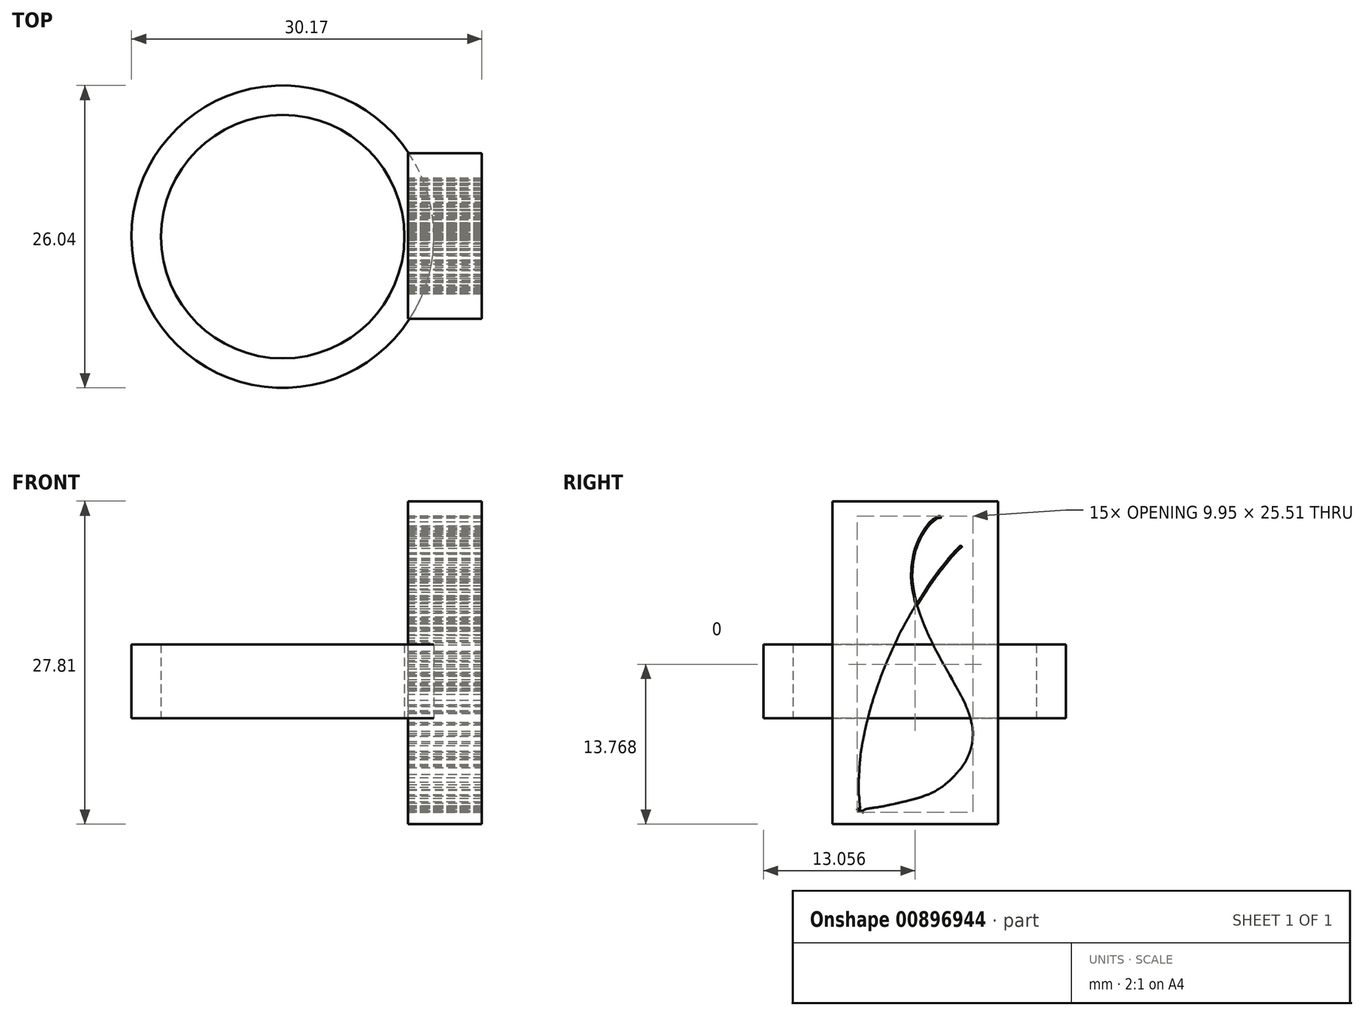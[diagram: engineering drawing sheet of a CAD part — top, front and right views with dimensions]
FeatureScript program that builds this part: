
annotation { "Feature Type Name" : "Feature", "Feature Type Description" : "" }
export const myFeature = defineFeature(function(context is Context, id is Id, definition is map)
    precondition{}
    {
        {
            var Q0;
            Q0=qCreatedBy(makeId("Top.planeOp"),FACE);
            var sketch = newSketch(context, id + "F0", { "sketchPlane" : qUnion([Q0])});
            skCircle(sketch, "E0", {"center": v(0, 0) * mm, "radius": 10.48 * mm});
            skCircle(sketch, "E1", {"center": v(0, 0) * mm, "radius": 13.02 * mm});
            skSolve(sketch);
        }
        {
            var Q0;
            Q0 = qSketchRegion(id + "F0", true);
            extrude(context, id + "F1", {"entities" : qUnion([Q0]), "depth" : 6.35 * mm, "offsetDistance" : 25.4 * mm});
        }
        {
            var Q0;
            Q0=qCreatedBy(makeId("Right.planeOp"),FACE);
            var sketch = newSketch(context, id + "F2", { "sketchPlane" : qUnion([Q0])});
            skLineSegment(sketch, "E2", {"start": v(0.02, 4.98) * mm, "end": v(0.1, 5.1) * mm});
            skLineSegment(sketch, "E3", {"start": v(0.1, 5.1) * mm, "end": v(0.07, 5.2) * mm});
            skLineSegment(sketch, "E4", {"start": v(0.07, 5.2) * mm, "end": v(0.02, 4.98) * mm});
            skLineSegment(sketch, "E5", {"start": v(-4.25, -12.47) * mm, "end": v(-4.48, -12.52) * mm});
            skLineSegment(sketch, "E6", {"start": v(-4.48, -12.52) * mm, "end": v(-4.48, -12.6) * mm});
            skLineSegment(sketch, "E7", {"start": v(-4.48, -12.6) * mm, "end": v(-4.25, -12.47) * mm});
            skFitSpline(sketch, "E8", {"points": [v(-4.5, -12.72) * mm, v(-4.5, -12.7) * mm, v(-4.52, -12.7) * mm, v(-4.52, -12.68) * mm]});
            skFitSpline(sketch, "E9", {"points": [v(-4.52, -12.68) * mm, v(-4.52, -12.67) * mm, v(-4.53, -12.66) * mm, v(-4.55, -12.65) * mm]});
            skFitSpline(sketch, "E10", {"points": [v(-4.55, -12.65) * mm, v(-4.57, -12.64) * mm, v(-4.6, -12.61) * mm, v(-4.62, -12.58) * mm]});
            skFitSpline(sketch, "E11", {"points": [v(-4.62, -12.58) * mm, v(-4.66, -12.53) * mm, v(-4.66, -12.52) * mm, v(-4.71, -12.55) * mm]});
            skFitSpline(sketch, "E12", {"points": [v(-4.71, -12.55) * mm, v(-4.76, -12.56) * mm, v(-4.75, -12.6) * mm, v(-4.7, -12.63) * mm]});
            skFitSpline(sketch, "E13", {"points": [v(-4.7, -12.63) * mm, v(-4.65, -12.64) * mm, v(-4.65, -12.67) * mm, v(-4.68, -12.69) * mm]});
            skFitSpline(sketch, "E14", {"points": [v(-4.68, -12.69) * mm, v(-4.7, -12.7) * mm, v(-4.73, -12.67) * mm, v(-4.77, -12.65) * mm]});
            skFitSpline(sketch, "E15", {"points": [v(-4.77, -12.65) * mm, v(-4.8, -12.62) * mm, v(-4.85, -12.59) * mm, v(-4.88, -12.57) * mm]});
            skFitSpline(sketch, "E16", {"points": [v(-4.88, -12.57) * mm, v(-4.92, -12.55) * mm, v(-4.94, -12.53) * mm, v(-4.94, -12.5) * mm]});
            skFitSpline(sketch, "E17", {"points": [v(-4.94, -12.5) * mm, v(-4.94, -12.46) * mm, v(-4.93, -12.45) * mm, v(-4.8, -12.41) * mm]});
            skFitSpline(sketch, "E18", {"points": [v(-4.8, -12.41) * mm, v(-4.7, -12.38) * mm, v(-4.69, -12.37) * mm, v(-4.72, -12.22) * mm]});
            skFitSpline(sketch, "E19", {"points": [v(-4.72, -12.22) * mm, v(-4.73, -12.16) * mm, v(-4.75, -11.95) * mm, v(-4.76, -11.75) * mm]});
            skFitSpline(sketch, "E20", {"points": [v(-4.76, -11.75) * mm, v(-4.77, -11.56) * mm, v(-4.78, -11.36) * mm, v(-4.8, -11.3) * mm]});
            skFitSpline(sketch, "E21", {"points": [v(-4.8, -11.3) * mm, v(-4.81, -11.17) * mm, v(-4.82, -10.04) * mm, v(-4.8, -9.78) * mm]});
            skFitSpline(sketch, "E22", {"points": [v(-4.8, -9.78) * mm, v(-4.8, -9.6) * mm, v(-4.79, -9.5) * mm, v(-4.76, -9.07) * mm]});
            skFitSpline(sketch, "E23", {"points": [v(-4.76, -9.07) * mm, v(-4.75, -8.84) * mm, v(-4.73, -8.53) * mm, v(-4.7, -8.34) * mm]});
            skFitSpline(sketch, "E24", {"points": [v(-4.7, -8.34) * mm, v(-4.7, -8.25) * mm, v(-4.69, -8.1) * mm, v(-4.68, -8) * mm]});
            skFitSpline(sketch, "E25", {"points": [v(-4.68, -8) * mm, v(-4.67, -7.89) * mm, v(-4.66, -7.78) * mm, v(-4.65, -7.75) * mm]});
            skFitSpline(sketch, "E26", {"points": [v(-4.65, -7.75) * mm, v(-4.65, -7.72) * mm, v(-4.64, -7.63) * mm, v(-4.63, -7.55) * mm]});
            skFitSpline(sketch, "E27", {"points": [v(-4.63, -7.55) * mm, v(-4.62, -7.47) * mm, v(-4.6, -7.34) * mm, v(-4.58, -7.25) * mm]});
            skFitSpline(sketch, "E28", {"points": [v(-4.58, -7.25) * mm, v(-4.56, -7.17) * mm, v(-4.54, -7.05) * mm, v(-4.53, -6.98) * mm]});
            skFitSpline(sketch, "E29", {"points": [v(-4.53, -6.98) * mm, v(-4.52, -6.91) * mm, v(-4.51, -6.83) * mm, v(-4.5, -6.8) * mm]});
            skFitSpline(sketch, "E30", {"points": [v(-4.5, -6.8) * mm, v(-4.5, -6.77) * mm, v(-4.48, -6.7) * mm, v(-4.47, -6.63) * mm]});
            skFitSpline(sketch, "E31", {"points": [v(-4.47, -6.63) * mm, v(-4.44, -6.51) * mm, v(-4.43, -6.46) * mm, v(-4.39, -6.23) * mm]});
            skFitSpline(sketch, "E32", {"points": [v(-4.39, -6.23) * mm, v(-4.38, -6.18) * mm, v(-4.36, -6.12) * mm, v(-4.36, -6.1) * mm]});
            skFitSpline(sketch, "E33", {"points": [v(-4.36, -6.1) * mm, v(-4.35, -6.07) * mm, v(-4.34, -6) * mm, v(-4.33, -5.95) * mm]});
            skFitSpline(sketch, "E34", {"points": [v(-4.33, -5.95) * mm, v(-4.33, -5.9) * mm, v(-4.31, -5.81) * mm, v(-4.3, -5.76) * mm]});
            skFitSpline(sketch, "E35", {"points": [v(-4.3, -5.76) * mm, v(-4.28, -5.68) * mm, v(-4.25, -5.55) * mm, v(-4.18, -5.24) * mm]});
            skFitSpline(sketch, "E36", {"points": [v(-4.18, -5.24) * mm, v(-4.16, -5.15) * mm, v(-4.13, -5.02) * mm, v(-4.1, -4.94) * mm]});
            skFitSpline(sketch, "E37", {"points": [v(-4.1, -4.94) * mm, v(-4.05, -4.75) * mm, v(-3.99, -4.47) * mm, v(-3.98, -4.4) * mm]});
            skFitSpline(sketch, "E38", {"points": [v(-3.98, -4.4) * mm, v(-3.97, -4.38) * mm, v(-3.96, -4.35) * mm, v(-3.95, -4.35) * mm]});
            skFitSpline(sketch, "E39", {"points": [v(-3.95, -4.35) * mm, v(-3.95, -4.34) * mm, v(-3.94, -4.32) * mm, v(-3.94, -4.3) * mm]});
            skFitSpline(sketch, "E40", {"points": [v(-3.94, -4.3) * mm, v(-3.94, -4.28) * mm, v(-3.93, -4.25) * mm, v(-3.93, -4.22) * mm]});
            skFitSpline(sketch, "E41", {"points": [v(-3.93, -4.22) * mm, v(-3.92, -4.2) * mm, v(-3.9, -4.16) * mm, v(-3.9, -4.12) * mm]});
            skFitSpline(sketch, "E42", {"points": [v(-3.9, -4.12) * mm, v(-3.89, -4.09) * mm, v(-3.86, -4) * mm, v(-3.84, -3.92) * mm]});
            skFitSpline(sketch, "E43", {"points": [v(-3.84, -3.92) * mm, v(-3.82, -3.84) * mm, v(-3.78, -3.71) * mm, v(-3.76, -3.64) * mm]});
            skFitSpline(sketch, "E44", {"points": [v(-3.76, -3.64) * mm, v(-3.74, -3.56) * mm, v(-3.72, -3.49) * mm, v(-3.72, -3.48) * mm]});
            skFitSpline(sketch, "E45", {"points": [v(-3.72, -3.48) * mm, v(-3.64, -3.26) * mm, v(-3.6, -3.14) * mm, v(-3.6, -3.12) * mm]});
            skFitSpline(sketch, "E46", {"points": [v(-3.6, -3.12) * mm, v(-3.6, -3.1) * mm, v(-3.47, -2.68) * mm, v(-3.44, -2.6) * mm]});
            skFitSpline(sketch, "E47", {"points": [v(-3.44, -2.6) * mm, v(-3.4, -2.52) * mm, v(-3.34, -2.32) * mm, v(-3.33, -2.26) * mm]});
            skFitSpline(sketch, "E48", {"points": [v(-3.33, -2.26) * mm, v(-3.32, -2.22) * mm, v(-3.3, -2.17) * mm, v(-3.29, -2.15) * mm]});
            skFitSpline(sketch, "E49", {"points": [v(-3.29, -2.15) * mm, v(-3.28, -2.13) * mm, v(-3.27, -2.1) * mm, v(-3.27, -2.09) * mm]});
            skFitSpline(sketch, "E50", {"points": [v(-3.27, -2.09) * mm, v(-3.27, -2.07) * mm, v(-3.26, -2.04) * mm, v(-3.25, -2.02) * mm]});
            skFitSpline(sketch, "E51", {"points": [v(-3.25, -2.02) * mm, v(-3.24, -2) * mm, v(-3.21, -1.92) * mm, v(-3.18, -1.84) * mm]});
            skFitSpline(sketch, "E52", {"points": [v(-3.18, -1.84) * mm, v(-3.15, -1.75) * mm, v(-3.08, -1.54) * mm, v(-3.02, -1.37) * mm]});
            skFitSpline(sketch, "E53", {"points": [v(-3.02, -1.37) * mm, v(-2.96, -1.2) * mm, v(-2.9, -1.04) * mm, v(-2.9, -1.01) * mm]});
            skFitSpline(sketch, "E54", {"points": [v(-2.9, -1.01) * mm, v(-2.89, -0.98) * mm, v(-2.87, -0.95) * mm, v(-2.87, -0.94) * mm]});
            skFitSpline(sketch, "E55", {"points": [v(-2.87, -0.94) * mm, v(-2.86, -0.93) * mm, v(-2.85, -0.92) * mm, v(-2.85, -0.9) * mm]});
            skFitSpline(sketch, "E56", {"points": [v(-2.85, -0.9) * mm, v(-2.85, -0.9) * mm, v(-2.84, -0.84) * mm, v(-2.81, -0.8) * mm]});
            skFitSpline(sketch, "E57", {"points": [v(-2.81, -0.8) * mm, v(-2.8, -0.75) * mm, v(-2.75, -0.66) * mm, v(-2.73, -0.58) * mm]});
            skFitSpline(sketch, "E58", {"points": [v(-2.73, -0.58) * mm, v(-2.7, -0.5) * mm, v(-2.66, -0.41) * mm, v(-2.64, -0.37) * mm]});
            skFitSpline(sketch, "E59", {"points": [v(-2.64, -0.37) * mm, v(-2.62, -0.33) * mm, v(-2.6, -0.26) * mm, v(-2.58, -0.22) * mm]});
            skFitSpline(sketch, "E60", {"points": [v(-2.58, -0.22) * mm, v(-2.55, -0.15) * mm, v(-2.47, 0.05) * mm, v(-2.39, 0.23) * mm]});
            skFitSpline(sketch, "E61", {"points": [v(-2.39, 0.23) * mm, v(-2.37, 0.27) * mm, v(-2.36, 0.3) * mm, v(-2.36, 0.31) * mm]});
            skFitSpline(sketch, "E62", {"points": [v(-2.36, 0.31) * mm, v(-2.36, 0.32) * mm, v(-2.34, 0.35) * mm, v(-2.32, 0.38) * mm]});
            skFitSpline(sketch, "E63", {"points": [v(-2.32, 0.38) * mm, v(-2.3, 0.42) * mm, v(-2.28, 0.48) * mm, v(-2.26, 0.53) * mm]});
            skFitSpline(sketch, "E64", {"points": [v(-2.26, 0.53) * mm, v(-2.24, 0.57) * mm, v(-2.2, 0.66) * mm, v(-2.16, 0.74) * mm]});
            skFitSpline(sketch, "E65", {"points": [v(-2.16, 0.74) * mm, v(-2.13, 0.8) * mm, v(-2.1, 0.87) * mm, v(-2.1, 0.88) * mm]});
            skFitSpline(sketch, "E66", {"points": [v(-2.1, 0.88) * mm, v(-2.1, 0.9) * mm, v(-2.09, 0.91) * mm, v(-2.08, 0.92) * mm]});
            skFitSpline(sketch, "E67", {"points": [v(-2.08, 0.92) * mm, v(-2.06, 0.93) * mm, v(-2.06, 0.95) * mm, v(-2.06, 0.96) * mm]});
            skFitSpline(sketch, "E68", {"points": [v(-2.06, 0.96) * mm, v(-2.07, 0.96) * mm, v(-2.06, 0.98) * mm, v(-2.05, 1) * mm]});
            skFitSpline(sketch, "E69", {"points": [v(-2.05, 1) * mm, v(-2.05, 1.01) * mm, v(-2.01, 1.08) * mm, v(-1.98, 1.15) * mm]});
            skFitSpline(sketch, "E70", {"points": [v(-1.98, 1.15) * mm, v(-1.9, 1.33) * mm, v(-1.88, 1.38) * mm, v(-1.77, 1.61) * mm]});
            skFitSpline(sketch, "E71", {"points": [v(-1.77, 1.61) * mm, v(-1.72, 1.72) * mm, v(-1.66, 1.84) * mm, v(-1.64, 1.88) * mm]});
            skFitSpline(sketch, "E72", {"points": [v(-1.64, 1.88) * mm, v(-1.63, 1.92) * mm, v(-1.6, 1.97) * mm, v(-1.6, 1.98) * mm]});
            skFitSpline(sketch, "E73", {"points": [v(-1.6, 1.98) * mm, v(-1.58, 2) * mm, v(-1.57, 2) * mm, v(-1.57, 2.02) * mm]});
            skFitSpline(sketch, "E74", {"points": [v(-1.57, 2.02) * mm, v(-1.57, 2.02) * mm, v(-1.55, 2.07) * mm, v(-1.52, 2.13) * mm]});
            skFitSpline(sketch, "E75", {"points": [v(-1.52, 2.13) * mm, v(-1.5, 2.19) * mm, v(-1.48, 2.24) * mm, v(-1.48, 2.25) * mm]});
            skFitSpline(sketch, "E76", {"points": [v(-1.48, 2.25) * mm, v(-1.48, 2.25) * mm, v(-1.23, 2.76) * mm, v(-1.2, 2.82) * mm]});
            skFitSpline(sketch, "E77", {"points": [v(-1.2, 2.82) * mm, v(-1.2, 2.84) * mm, v(-1.16, 2.9) * mm, v(-1.14, 2.94) * mm]});
            skFitSpline(sketch, "E78", {"points": [v(-1.14, 2.94) * mm, v(-1.1, 2.99) * mm, v(-1.08, 3.05) * mm, v(-1.06, 3.07) * mm]});
            skFitSpline(sketch, "E79", {"points": [v(-1.06, 3.07) * mm, v(-1.04, 3.1) * mm, v(-1.03, 3.12) * mm, v(-1.03, 3.13) * mm]});
            skFitSpline(sketch, "E80", {"points": [v(-1.03, 3.13) * mm, v(-1.03, 3.15) * mm, v(-1.02, 3.16) * mm, v(-1.01, 3.17) * mm]});
            skFitSpline(sketch, "E81", {"points": [v(-1.01, 3.17) * mm, v(-1, 3.2) * mm, v(-0.95, 3.27) * mm, v(-0.85, 3.46) * mm]});
            skFitSpline(sketch, "E82", {"points": [v(-0.85, 3.46) * mm, v(-0.8, 3.55) * mm, v(-0.75, 3.65) * mm, v(-0.72, 3.7) * mm]});
            skFitSpline(sketch, "E83", {"points": [v(-0.72, 3.7) * mm, v(-0.69, 3.75) * mm, v(-0.66, 3.8) * mm, v(-0.66, 3.8) * mm]});
            skFitSpline(sketch, "E84", {"points": [v(-0.66, 3.8) * mm, v(-0.66, 3.8) * mm, v(-0.63, 3.87) * mm, v(-0.59, 3.93) * mm]});
            skFitSpline(sketch, "E85", {"points": [v(-0.59, 3.93) * mm, v(-0.55, 4) * mm, v(-0.5, 4.08) * mm, v(-0.49, 4.1) * mm]});
            skFitSpline(sketch, "E86", {"points": [v(-0.49, 4.1) * mm, v(-0.44, 4.19) * mm, v(-0.36, 4.35) * mm, v(-0.34, 4.37) * mm]});
            skFitSpline(sketch, "E87", {"points": [v(-0.34, 4.37) * mm, v(-0.33, 4.38) * mm, v(-0.31, 4.42) * mm, v(-0.29, 4.46) * mm]});
            skFitSpline(sketch, "E88", {"points": [v(-0.29, 4.46) * mm, v(-0.2, 4.62) * mm, v(-0.16, 4.7) * mm, v(-0.1, 4.77) * mm]});
            skFitSpline(sketch, "E89", {"points": [v(-0.1, 4.77) * mm, v(-0.08, 4.8) * mm, v(-0.05, 4.85) * mm, v(-0.05, 4.85) * mm]});
            skFitSpline(sketch, "E90", {"points": [v(-0.05, 4.85) * mm, v(-0.05, 4.85) * mm, v(-0.02, 4.91) * mm, v(0.02, 4.98) * mm]});
            skFitSpline(sketch, "E91", {"points": [v(0.07, 5.2) * mm, v(0.05, 5.27) * mm, v(0.04, 5.34) * mm, v(0.03, 5.37) * mm]});
            skFitSpline(sketch, "E92", {"points": [v(0.03, 5.37) * mm, v(-0.01, 5.5) * mm, v(-0.04, 5.63) * mm, v(-0.04, 5.68) * mm]});
            skFitSpline(sketch, "E93", {"points": [v(-0.04, 5.68) * mm, v(-0.04, 5.72) * mm, v(-0.05, 5.75) * mm, v(-0.06, 5.76) * mm]});
            skFitSpline(sketch, "E94", {"points": [v(-0.06, 5.76) * mm, v(-0.07, 5.76) * mm, v(-0.07, 5.8) * mm, v(-0.07, 5.83) * mm]});
            skFitSpline(sketch, "E95", {"points": [v(-0.07, 5.83) * mm, v(-0.07, 5.86) * mm, v(-0.08, 5.9) * mm, v(-0.09, 5.93) * mm]});
            skFitSpline(sketch, "E96", {"points": [v(-0.09, 5.93) * mm, v(-0.1, 5.95) * mm, v(-0.1, 6) * mm, v(-0.1, 6.03) * mm]});
            skFitSpline(sketch, "E97", {"points": [v(-0.1, 6.03) * mm, v(-0.11, 6.06) * mm, v(-0.13, 6.12) * mm, v(-0.14, 6.15) * mm]});
            skFitSpline(sketch, "E98", {"points": [v(-0.14, 6.15) * mm, v(-0.16, 6.18) * mm, v(-0.16, 6.2) * mm, v(-0.16, 6.22) * mm]});
            skFitSpline(sketch, "E99", {"points": [v(-0.16, 6.22) * mm, v(-0.15, 6.22) * mm, v(-0.16, 6.27) * mm, v(-0.17, 6.32) * mm]});
            skFitSpline(sketch, "E100", {"points": [v(-0.17, 6.32) * mm, v(-0.18, 6.36) * mm, v(-0.2, 6.4) * mm, v(-0.19, 6.41) * mm]});
            skFitSpline(sketch, "E101", {"points": [v(-0.19, 6.41) * mm, v(-0.18, 6.42) * mm, v(-0.19, 6.44) * mm, v(-0.2, 6.47) * mm]});
            skFitSpline(sketch, "E102", {"points": [v(-0.2, 6.47) * mm, v(-0.21, 6.5) * mm, v(-0.23, 6.6) * mm, v(-0.23, 6.71) * mm]});
            skFitSpline(sketch, "E103", {"points": [v(-0.23, 6.71) * mm, v(-0.23, 6.74) * mm, v(-0.24, 6.76) * mm, v(-0.25, 6.76) * mm]});
            skFitSpline(sketch, "E104", {"points": [v(-0.25, 6.76) * mm, v(-0.25, 6.77) * mm, v(-0.26, 6.83) * mm, v(-0.27, 6.9) * mm]});
            skFitSpline(sketch, "E105", {"points": [v(-0.27, 6.9) * mm, v(-0.29, 7.23) * mm, v(-0.3, 7.32) * mm, v(-0.3, 7.34) * mm]});
            skFitSpline(sketch, "E106", {"points": [v(-0.3, 7.34) * mm, v(-0.32, 7.38) * mm, v(-0.3, 7.89) * mm, v(-0.28, 8.17) * mm]});
            skFitSpline(sketch, "E107", {"points": [v(-0.28, 8.17) * mm, v(-0.28, 8.24) * mm, v(-0.27, 8.31) * mm, v(-0.28, 8.34) * mm]});
            skFitSpline(sketch, "E108", {"points": [v(-0.28, 8.34) * mm, v(-0.28, 8.37) * mm, v(-0.27, 8.46) * mm, v(-0.25, 8.54) * mm]});
            skFitSpline(sketch, "E109", {"points": [v(-0.25, 8.54) * mm, v(-0.24, 8.62) * mm, v(-0.22, 8.73) * mm, v(-0.22, 8.77) * mm]});
            skFitSpline(sketch, "E110", {"points": [v(-0.22, 8.77) * mm, v(-0.22, 8.81) * mm, v(-0.2, 8.89) * mm, v(-0.2, 8.94) * mm]});
            skFitSpline(sketch, "E111", {"points": [v(-0.2, 8.94) * mm, v(-0.19, 8.99) * mm, v(-0.17, 9.07) * mm, v(-0.16, 9.13) * mm]});
            skFitSpline(sketch, "E112", {"points": [v(-0.16, 9.13) * mm, v(-0.13, 9.4) * mm, v(-0.1, 9.57) * mm, v(-0.08, 9.6) * mm]});
            skFitSpline(sketch, "E113", {"points": [v(-0.08, 9.6) * mm, v(-0.07, 9.6) * mm, v(-0.07, 9.63) * mm, v(-0.06, 9.65) * mm]});
            skFitSpline(sketch, "E114", {"points": [v(-0.06, 9.65) * mm, v(-0.05, 9.72) * mm, v(0.1, 10.2) * mm, v(0.14, 10.3) * mm]});
            skFitSpline(sketch, "E115", {"points": [v(0.14, 10.3) * mm, v(0.16, 10.33) * mm, v(0.18, 10.39) * mm, v(0.2, 10.43) * mm]});
            skFitSpline(sketch, "E116", {"points": [v(0.2, 10.43) * mm, v(0.28, 10.64) * mm, v(0.4, 10.9) * mm, v(0.48, 11.03) * mm]});
            skFitSpline(sketch, "E117", {"points": [v(0.48, 11.03) * mm, v(0.5, 11.07) * mm, v(0.55, 11.15) * mm, v(0.57, 11.2) * mm]});
            skFitSpline(sketch, "E118", {"points": [v(0.57, 11.2) * mm, v(0.6, 11.25) * mm, v(0.65, 11.35) * mm, v(0.7, 11.4) * mm]});
            skFitSpline(sketch, "E119", {"points": [v(0.7, 11.4) * mm, v(0.73, 11.47) * mm, v(0.79, 11.56) * mm, v(0.82, 11.62) * mm]});
            skFitSpline(sketch, "E120", {"points": [v(0.82, 11.62) * mm, v(0.85, 11.67) * mm, v(0.9, 11.75) * mm, v(0.94, 11.79) * mm]});
            skFitSpline(sketch, "E121", {"points": [v(0.94, 11.79) * mm, v(0.97, 11.82) * mm, v(1.03, 11.9) * mm, v(1.06, 11.95) * mm]});
            skFitSpline(sketch, "E122", {"points": [v(1.06, 11.95) * mm, v(1.24, 12.18) * mm, v(1.67, 12.54) * mm, v(1.9, 12.66) * mm]});
            skFitSpline(sketch, "E123", {"points": [v(1.9, 12.66) * mm, v(1.94, 12.67) * mm, v(1.99, 12.7) * mm, v(2, 12.71) * mm]});
            skFitSpline(sketch, "E124", {"points": [v(2, 12.71) * mm, v(2.06, 12.76) * mm, v(2.24, 12.73) * mm, v(2.26, 12.67) * mm]});
            skFitSpline(sketch, "E125", {"points": [v(2.26, 12.67) * mm, v(2.27, 12.63) * mm, v(2.2, 12.59) * mm, v(2.15, 12.6) * mm]});
            skFitSpline(sketch, "E126", {"points": [v(2.15, 12.6) * mm, v(2.05, 12.61) * mm, v(1.8, 12.47) * mm, v(1.57, 12.27) * mm]});
            skFitSpline(sketch, "E127", {"points": [v(1.57, 12.27) * mm, v(1.46, 12.17) * mm, v(1.23, 11.94) * mm, v(1.15, 11.84) * mm]});
            skFitSpline(sketch, "E128", {"points": [v(1.15, 11.84) * mm, v(1.11, 11.8) * mm, v(1.06, 11.74) * mm, v(1.04, 11.7) * mm]});
            skFitSpline(sketch, "E129", {"points": [v(1.04, 11.7) * mm, v(1.01, 11.67) * mm, v(0.97, 11.61) * mm, v(0.95, 11.57) * mm]});
            skFitSpline(sketch, "E130", {"points": [v(0.95, 11.57) * mm, v(0.92, 11.52) * mm, v(0.9, 11.47) * mm, v(0.88, 11.46) * mm]});
            skFitSpline(sketch, "E131", {"points": [v(0.88, 11.46) * mm, v(0.87, 11.45) * mm, v(0.84, 11.41) * mm, v(0.82, 11.37) * mm]});
            skFitSpline(sketch, "E132", {"points": [v(0.82, 11.37) * mm, v(0.8, 11.33) * mm, v(0.76, 11.29) * mm, v(0.75, 11.28) * mm]});
            skFitSpline(sketch, "E133", {"points": [v(0.75, 11.28) * mm, v(0.74, 11.27) * mm, v(0.73, 11.24) * mm, v(0.72, 11.22) * mm]});
            skFitSpline(sketch, "E134", {"points": [v(0.72, 11.22) * mm, v(0.72, 11.2) * mm, v(0.7, 11.16) * mm, v(0.67, 11.14) * mm]});
            skFitSpline(sketch, "E135", {"points": [v(0.67, 11.14) * mm, v(0.65, 11.11) * mm, v(0.62, 11.05) * mm, v(0.6, 11) * mm]});
            skFitSpline(sketch, "E136", {"points": [v(0.6, 11) * mm, v(0.57, 10.95) * mm, v(0.53, 10.89) * mm, v(0.5, 10.85) * mm]});
            skFitSpline(sketch, "E137", {"points": [v(0.5, 10.85) * mm, v(0.5, 10.82) * mm, v(0.48, 10.78) * mm, v(0.48, 10.78) * mm]});
            skFitSpline(sketch, "E138", {"points": [v(0.48, 10.78) * mm, v(0.48, 10.77) * mm, v(0.46, 10.74) * mm, v(0.44, 10.71) * mm]});
            skFitSpline(sketch, "E139", {"points": [v(0.44, 10.71) * mm, v(0.43, 10.69) * mm, v(0.42, 10.67) * mm, v(0.42, 10.66) * mm]});
            skFitSpline(sketch, "E140", {"points": [v(0.42, 10.66) * mm, v(0.42, 10.66) * mm, v(0.4, 10.6) * mm, v(0.36, 10.53) * mm]});
            skFitSpline(sketch, "E141", {"points": [v(0.36, 10.53) * mm, v(0.33, 10.46) * mm, v(0.3, 10.4) * mm, v(0.3, 10.38) * mm]});
            skFitSpline(sketch, "E142", {"points": [v(0.3, 10.38) * mm, v(0.3, 10.36) * mm, v(0.29, 10.34) * mm, v(0.28, 10.32) * mm]});
            skFitSpline(sketch, "E143", {"points": [v(0.28, 10.32) * mm, v(0.26, 10.3) * mm, v(0.25, 10.28) * mm, v(0.25, 10.27) * mm]});
            skFitSpline(sketch, "E144", {"points": [v(0.25, 10.27) * mm, v(0.25, 10.26) * mm, v(0.24, 10.22) * mm, v(0.23, 10.2) * mm]});
            skFitSpline(sketch, "E145", {"points": [v(0.23, 10.2) * mm, v(0.22, 10.17) * mm, v(0.2, 10.12) * mm, v(0.19, 10.08) * mm]});
            skFitSpline(sketch, "E146", {"points": [v(0.19, 10.08) * mm, v(0.18, 10.05) * mm, v(0.16, 10) * mm, v(0.15, 9.99) * mm]});
            skFitSpline(sketch, "E147", {"points": [v(0.15, 9.99) * mm, v(0.12, 9.91) * mm, v(0.03, 9.62) * mm, v(0.03, 9.59) * mm]});
            skFitSpline(sketch, "E148", {"points": [v(0.03, 9.59) * mm, v(0.03, 9.57) * mm, v(0.02, 9.52) * mm, v(0, 9.49) * mm]});
            skFitSpline(sketch, "E149", {"points": [v(0, 9.49) * mm, v(0, 9.45) * mm, v(-0.03, 9.35) * mm, v(-0.04, 9.25) * mm]});
            skFitSpline(sketch, "E150", {"points": [v(-0.04, 9.25) * mm, v(-0.06, 9.16) * mm, v(-0.08, 9.05) * mm, v(-0.08, 9.01) * mm]});
            skFitSpline(sketch, "E151", {"points": [v(-0.08, 9.01) * mm, v(-0.12, 8.87) * mm, v(-0.18, 8.26) * mm, v(-0.2, 7.92) * mm]});
            skFitSpline(sketch, "E152", {"points": [v(-0.2, 7.92) * mm, v(-0.21, 7.62) * mm, v(-0.21, 7.53) * mm, v(-0.2, 7.25) * mm]});
            skFitSpline(sketch, "E153", {"points": [v(-0.2, 7.25) * mm, v(-0.18, 7.07) * mm, v(-0.15, 6.87) * mm, v(-0.14, 6.79) * mm]});
            skFitSpline(sketch, "E154", {"points": [v(-0.14, 6.79) * mm, v(-0.11, 6.6) * mm, v(-0.1, 6.55) * mm, v(-0.08, 6.42) * mm]});
            skFitSpline(sketch, "E155", {"points": [v(-0.08, 6.42) * mm, v(-0.08, 6.36) * mm, v(-0.06, 6.27) * mm, v(-0.05, 6.21) * mm]});
            skFitSpline(sketch, "E156", {"points": [v(-0.05, 6.21) * mm, v(0, 6.02) * mm, v(0.02, 5.92) * mm, v(0.01, 5.9) * mm]});
            skFitSpline(sketch, "E157", {"points": [v(0.01, 5.9) * mm, v(0.01, 5.9) * mm, v(0.01, 5.88) * mm, v(0.02, 5.87) * mm]});
            skFitSpline(sketch, "E158", {"points": [v(0.02, 5.87) * mm, v(0.03, 5.85) * mm, v(0.04, 5.83) * mm, v(0.04, 5.82) * mm]});
            skFitSpline(sketch, "E159", {"points": [v(0.04, 5.82) * mm, v(0.04, 5.8) * mm, v(0.06, 5.72) * mm, v(0.07, 5.63) * mm]});
            skFitSpline(sketch, "E160", {"points": [v(0.07, 5.63) * mm, v(0.13, 5.35) * mm, v(0.15, 5.27) * mm, v(0.17, 5.26) * mm]});
            skFitSpline(sketch, "E161", {"points": [v(0.17, 5.26) * mm, v(0.19, 5.26) * mm, v(0.22, 5.3) * mm, v(0.35, 5.5) * mm]});
            skFitSpline(sketch, "E162", {"points": [v(0.35, 5.5) * mm, v(0.4, 5.58) * mm, v(0.48, 5.7) * mm, v(0.53, 5.79) * mm]});
            skFitSpline(sketch, "E163", {"points": [v(0.53, 5.79) * mm, v(0.73, 6.08) * mm, v(0.84, 6.26) * mm, v(0.88, 6.34) * mm]});
            skFitSpline(sketch, "E164", {"points": [v(0.88, 6.34) * mm, v(0.92, 6.41) * mm, v(1.04, 6.6) * mm, v(1.23, 6.89) * mm]});
            skFitSpline(sketch, "E165", {"points": [v(1.23, 6.89) * mm, v(1.34, 7.07) * mm, v(1.45, 7.23) * mm, v(1.51, 7.3) * mm]});
            skFitSpline(sketch, "E166", {"points": [v(1.51, 7.3) * mm, v(1.54, 7.32) * mm, v(1.56, 7.35) * mm, v(1.56, 7.36) * mm]});
            skFitSpline(sketch, "E167", {"points": [v(1.56, 7.36) * mm, v(1.56, 7.36) * mm, v(1.62, 7.44) * mm, v(1.69, 7.53) * mm]});
            skFitSpline(sketch, "E168", {"points": [v(1.69, 7.53) * mm, v(1.76, 7.62) * mm, v(1.82, 7.7) * mm, v(1.83, 7.72) * mm]});
            skFitSpline(sketch, "E169", {"points": [v(1.83, 7.72) * mm, v(1.86, 7.79) * mm, v(1.96, 7.92) * mm, v(2.11, 8.1) * mm]});
            skFitSpline(sketch, "E170", {"points": [v(2.11, 8.1) * mm, v(2.2, 8.22) * mm, v(2.3, 8.36) * mm, v(2.35, 8.42) * mm]});
            skFitSpline(sketch, "E171", {"points": [v(2.35, 8.42) * mm, v(2.4, 8.48) * mm, v(2.52, 8.62) * mm, v(2.6, 8.74) * mm]});
            skFitSpline(sketch, "E172", {"points": [v(2.6, 8.74) * mm, v(2.7, 8.85) * mm, v(2.82, 9.01) * mm, v(2.89, 9.1) * mm]});
            skFitSpline(sketch, "E173", {"points": [v(2.89, 9.1) * mm, v(2.95, 9.18) * mm, v(3.06, 9.31) * mm, v(3.14, 9.39) * mm]});
            skFitSpline(sketch, "E174", {"points": [v(3.14, 9.39) * mm, v(3.2, 9.46) * mm, v(3.3, 9.56) * mm, v(3.34, 9.6) * mm]});
            skFitSpline(sketch, "E175", {"points": [v(3.34, 9.6) * mm, v(3.38, 9.66) * mm, v(3.53, 9.81) * mm, v(3.66, 9.95) * mm]});
            skFitSpline(sketch, "E176", {"points": [v(3.66, 9.95) * mm, v(3.9, 10.2) * mm, v(3.91, 10.2) * mm, v(3.97, 10.2) * mm]});
            skFitSpline(sketch, "E177", {"points": [v(3.97, 10.2) * mm, v(4.02, 10.2) * mm, v(4.04, 10.19) * mm, v(4.04, 10.16) * mm]});
            skFitSpline(sketch, "E178", {"points": [v(4.04, 10.16) * mm, v(4.05, 10.1) * mm, v(4.03, 10.06) * mm, v(3.96, 10.01) * mm]});
            skFitSpline(sketch, "E179", {"points": [v(3.96, 10.01) * mm, v(3.87, 9.95) * mm, v(3.6, 9.69) * mm, v(3.46, 9.52) * mm]});
            skFitSpline(sketch, "E180", {"points": [v(3.46, 9.52) * mm, v(3.4, 9.45) * mm, v(3.3, 9.34) * mm, v(3.23, 9.27) * mm]});
            skFitSpline(sketch, "E181", {"points": [v(3.23, 9.27) * mm, v(3.17, 9.2) * mm, v(3.07, 9.09) * mm, v(3, 9) * mm]});
            skFitSpline(sketch, "E182", {"points": [v(3, 9) * mm, v(2.82, 8.77) * mm, v(2.76, 8.7) * mm, v(2.67, 8.6) * mm]});
            skFitSpline(sketch, "E183", {"points": [v(2.67, 8.6) * mm, v(2.63, 8.54) * mm, v(2.55, 8.44) * mm, v(2.5, 8.36) * mm]});
            skFitSpline(sketch, "E184", {"points": [v(2.5, 8.36) * mm, v(2.44, 8.3) * mm, v(2.33, 8.16) * mm, v(2.26, 8.07) * mm]});
            skFitSpline(sketch, "E185", {"points": [v(2.26, 8.07) * mm, v(2.18, 7.98) * mm, v(2.1, 7.87) * mm, v(2.06, 7.82) * mm]});
            skFitSpline(sketch, "E186", {"points": [v(2.06, 7.82) * mm, v(2.03, 7.77) * mm, v(1.98, 7.7) * mm, v(1.95, 7.66) * mm]});
            skFitSpline(sketch, "E187", {"points": [v(1.95, 7.66) * mm, v(1.88, 7.58) * mm, v(1.8, 7.47) * mm, v(1.71, 7.34) * mm]});
            skFitSpline(sketch, "E188", {"points": [v(1.71, 7.34) * mm, v(1.68, 7.29) * mm, v(1.62, 7.21) * mm, v(1.58, 7.17) * mm]});
            skFitSpline(sketch, "E189", {"points": [v(1.58, 7.17) * mm, v(1.55, 7.13) * mm, v(1.51, 7.08) * mm, v(1.51, 7.08) * mm]});
            skFitSpline(sketch, "E190", {"points": [v(1.51, 7.08) * mm, v(1.51, 7.07) * mm, v(1.49, 7.03) * mm, v(1.45, 6.98) * mm]});
            skFitSpline(sketch, "E191", {"points": [v(1.45, 6.98) * mm, v(1.38, 6.88) * mm, v(1.25, 6.68) * mm, v(1.04, 6.35) * mm]});
            skFitSpline(sketch, "E192", {"points": [v(1.04, 6.35) * mm, v(0.96, 6.23) * mm, v(0.83, 6.02) * mm, v(0.74, 5.88) * mm]});
            skFitSpline(sketch, "E193", {"points": [v(0.74, 5.88) * mm, v(0.65, 5.74) * mm, v(0.57, 5.62) * mm, v(0.57, 5.61) * mm]});
            skFitSpline(sketch, "E194", {"points": [v(0.57, 5.61) * mm, v(0.57, 5.6) * mm, v(0.56, 5.59) * mm, v(0.54, 5.57) * mm]});
            skFitSpline(sketch, "E195", {"points": [v(0.54, 5.57) * mm, v(0.52, 5.55) * mm, v(0.5, 5.54) * mm, v(0.5, 5.53) * mm]});
            skFitSpline(sketch, "E196", {"points": [v(0.5, 5.53) * mm, v(0.5, 5.52) * mm, v(0.42, 5.38) * mm, v(0.32, 5.22) * mm]});
            skFitSpline(sketch, "E197", {"points": [v(0.32, 5.22) * mm, v(0.22, 5.08) * mm, v(0.22, 5.06) * mm, v(0.25, 4.94) * mm]});
            skFitSpline(sketch, "E198", {"points": [v(0.25, 4.94) * mm, v(0.27, 4.88) * mm, v(0.3, 4.81) * mm, v(0.3, 4.79) * mm]});
            skFitSpline(sketch, "E199", {"points": [v(0.3, 4.79) * mm, v(0.32, 4.76) * mm, v(0.35, 4.66) * mm, v(0.38, 4.57) * mm]});
            skFitSpline(sketch, "E200", {"points": [v(0.38, 4.57) * mm, v(0.4, 4.48) * mm, v(0.44, 4.37) * mm, v(0.46, 4.32) * mm]});
            skFitSpline(sketch, "E201", {"points": [v(0.46, 4.32) * mm, v(0.53, 4.13) * mm, v(0.58, 4.01) * mm, v(0.6, 3.97) * mm]});
            skFitSpline(sketch, "E202", {"points": [v(0.6, 3.97) * mm, v(0.62, 3.91) * mm, v(0.67, 3.79) * mm, v(0.68, 3.75) * mm]});
            skFitSpline(sketch, "E203", {"points": [v(0.68, 3.75) * mm, v(0.69, 3.71) * mm, v(0.7, 3.69) * mm, v(0.74, 3.6) * mm]});
            skFitSpline(sketch, "E204", {"points": [v(0.74, 3.6) * mm, v(0.75, 3.56) * mm, v(0.76, 3.52) * mm, v(0.77, 3.5) * mm]});
            skFitSpline(sketch, "E205", {"points": [v(0.77, 3.5) * mm, v(0.78, 3.46) * mm, v(0.8, 3.42) * mm, v(0.88, 3.25) * mm]});
            skFitSpline(sketch, "E206", {"points": [v(0.88, 3.25) * mm, v(0.9, 3.21) * mm, v(0.9, 3.18) * mm, v(0.9, 3.17) * mm]});
            skFitSpline(sketch, "E207", {"points": [v(0.9, 3.17) * mm, v(0.9, 3.17) * mm, v(0.93, 3.1) * mm, v(0.96, 3.04) * mm]});
            skFitSpline(sketch, "E208", {"points": [v(0.96, 3.04) * mm, v(1, 2.97) * mm, v(1.03, 2.9) * mm, v(1.03, 2.88) * mm]});
            skFitSpline(sketch, "E209", {"points": [v(1.03, 2.88) * mm, v(1.14, 2.62) * mm, v(1.17, 2.55) * mm, v(1.18, 2.55) * mm]});
            skFitSpline(sketch, "E210", {"points": [v(1.18, 2.55) * mm, v(1.19, 2.54) * mm, v(1.2, 2.52) * mm, v(1.2, 2.5) * mm]});
            skFitSpline(sketch, "E211", {"points": [v(1.2, 2.5) * mm, v(1.2, 2.5) * mm, v(1.23, 2.4) * mm, v(1.28, 2.31) * mm]});
            skFitSpline(sketch, "E212", {"points": [v(1.28, 2.31) * mm, v(1.38, 2.14) * mm, v(1.54, 1.81) * mm, v(1.6, 1.7) * mm]});
            skFitSpline(sketch, "E213", {"points": [v(1.6, 1.7) * mm, v(1.64, 1.57) * mm, v(1.74, 1.39) * mm, v(1.8, 1.28) * mm]});
            skFitSpline(sketch, "E214", {"points": [v(1.8, 1.28) * mm, v(1.92, 1.04) * mm, v(1.98, 0.93) * mm, v(2, 0.91) * mm]});
            skFitSpline(sketch, "E215", {"points": [v(2, 0.91) * mm, v(2, 0.9) * mm, v(2.08, 0.77) * mm, v(2.16, 0.61) * mm]});
            skFitSpline(sketch, "E216", {"points": [v(2.16, 0.61) * mm, v(2.24, 0.45) * mm, v(2.3, 0.32) * mm, v(2.32, 0.3) * mm]});
            skFitSpline(sketch, "E217", {"points": [v(2.32, 0.3) * mm, v(2.32, 0.3) * mm, v(2.35, 0.26) * mm, v(2.37, 0.22) * mm]});
            skFitSpline(sketch, "E218", {"points": [v(2.37, 0.22) * mm, v(2.43, 0.1) * mm, v(2.48, 0.02) * mm, v(2.5, -0.02) * mm]});
            skFitSpline(sketch, "E219", {"points": [v(2.5, -0.02) * mm, v(2.53, -0.05) * mm, v(2.54, -0.07) * mm, v(2.54, -0.08) * mm]});
            skFitSpline(sketch, "E220", {"points": [v(2.54, -0.08) * mm, v(2.54, -0.08) * mm, v(2.56, -0.12) * mm, v(2.59, -0.16) * mm]});
            skFitSpline(sketch, "E221", {"points": [v(2.59, -0.16) * mm, v(2.61, -0.2) * mm, v(2.63, -0.23) * mm, v(2.63, -0.24) * mm]});
            skFitSpline(sketch, "E222", {"points": [v(2.63, -0.24) * mm, v(2.63, -0.24) * mm, v(2.68, -0.32) * mm, v(2.73, -0.42) * mm]});
            skFitSpline(sketch, "E223", {"points": [v(2.73, -0.42) * mm, v(2.79, -0.51) * mm, v(2.85, -0.63) * mm, v(2.88, -0.68) * mm]});
            skFitSpline(sketch, "E224", {"points": [v(2.88, -0.68) * mm, v(2.9, -0.73) * mm, v(2.94, -0.79) * mm, v(2.95, -0.81) * mm]});
            skFitSpline(sketch, "E225", {"points": [v(2.95, -0.81) * mm, v(2.97, -0.84) * mm, v(3, -0.9) * mm, v(3.02, -0.93) * mm]});
            skFitSpline(sketch, "E226", {"points": [v(3.02, -0.93) * mm, v(3.1, -1.06) * mm, v(3.2, -1.24) * mm, v(3.23, -1.3) * mm]});
            skFitSpline(sketch, "E227", {"points": [v(3.23, -1.3) * mm, v(3.25, -1.33) * mm, v(3.3, -1.43) * mm, v(3.33, -1.5) * mm]});
            skFitSpline(sketch, "E228", {"points": [v(3.33, -1.5) * mm, v(3.38, -1.6) * mm, v(3.41, -1.66) * mm, v(3.42, -1.67) * mm]});
            skFitSpline(sketch, "E229", {"points": [v(3.42, -1.67) * mm, v(3.42, -1.67) * mm, v(3.44, -1.71) * mm, v(3.46, -1.75) * mm]});
            skFitSpline(sketch, "E230", {"points": [v(3.46, -1.75) * mm, v(3.49, -1.8) * mm, v(3.5, -1.83) * mm, v(3.52, -1.83) * mm]});
            skFitSpline(sketch, "E231", {"points": [v(3.52, -1.83) * mm, v(3.52, -1.83) * mm, v(3.53, -1.84) * mm, v(3.53, -1.85) * mm]});
            skFitSpline(sketch, "E232", {"points": [v(3.53, -1.85) * mm, v(3.53, -1.86) * mm, v(3.57, -1.94) * mm, v(3.62, -2.02) * mm]});
            skFitSpline(sketch, "E233", {"points": [v(3.62, -2.02) * mm, v(3.67, -2.1) * mm, v(3.7, -2.17) * mm, v(3.7, -2.17) * mm]});
            skFitSpline(sketch, "E234", {"points": [v(3.7, -2.17) * mm, v(3.7, -2.17) * mm, v(3.74, -2.24) * mm, v(3.78, -2.31) * mm]});
            skFitSpline(sketch, "E235", {"points": [v(3.78, -2.31) * mm, v(3.88, -2.49) * mm, v(4.4, -3.52) * mm, v(4.4, -3.55) * mm]});
            skFitSpline(sketch, "E236", {"points": [v(4.4, -3.55) * mm, v(4.4, -3.55) * mm, v(4.41, -3.6) * mm, v(4.43, -3.64) * mm]});
            skFitSpline(sketch, "E237", {"points": [v(4.43, -3.64) * mm, v(4.53, -3.86) * mm, v(4.57, -3.94) * mm, v(4.58, -4) * mm]});
            skFitSpline(sketch, "E238", {"points": [v(4.58, -4) * mm, v(4.6, -4.04) * mm, v(4.61, -4.1) * mm, v(4.62, -4.1) * mm]});
            skFitSpline(sketch, "E239", {"points": [v(4.62, -4.1) * mm, v(4.67, -4.23) * mm, v(4.87, -4.95) * mm, v(4.87, -5.02) * mm]});
            skFitSpline(sketch, "E240", {"points": [v(4.87, -5.02) * mm, v(4.87, -5.04) * mm, v(4.88, -5.08) * mm, v(4.9, -5.1) * mm]});
            skFitSpline(sketch, "E241", {"points": [v(4.9, -5.1) * mm, v(4.94, -5.19) * mm, v(5.01, -5.96) * mm, v(5, -6.24) * mm]});
            skFitSpline(sketch, "E242", {"points": [v(5, -6.24) * mm, v(4.98, -6.52) * mm, v(4.94, -6.84) * mm, v(4.9, -7.01) * mm]});
            skFitSpline(sketch, "E243", {"points": [v(4.9, -7.01) * mm, v(4.85, -7.19) * mm, v(4.79, -7.43) * mm, v(4.76, -7.48) * mm]});
            skFitSpline(sketch, "E244", {"points": [v(4.76, -7.48) * mm, v(4.75, -7.5) * mm, v(4.74, -7.53) * mm, v(4.74, -7.56) * mm]});
            skFitSpline(sketch, "E245", {"points": [v(4.74, -7.56) * mm, v(4.73, -7.6) * mm, v(4.69, -7.7) * mm, v(4.61, -7.87) * mm]});
            skFitSpline(sketch, "E246", {"points": [v(4.61, -7.87) * mm, v(4.6, -7.91) * mm, v(4.57, -7.95) * mm, v(4.57, -7.95) * mm]});
            skFitSpline(sketch, "E247", {"points": [v(4.57, -7.95) * mm, v(4.56, -7.96) * mm, v(4.55, -7.97) * mm, v(4.55, -7.98) * mm]});
            skFitSpline(sketch, "E248", {"points": [v(4.55, -7.98) * mm, v(4.55, -8) * mm, v(4.54, -8.03) * mm, v(4.53, -8.05) * mm]});
            skFitSpline(sketch, "E249", {"points": [v(4.53, -8.05) * mm, v(4.52, -8.07) * mm, v(4.5, -8.11) * mm, v(4.49, -8.14) * mm]});
            skFitSpline(sketch, "E250", {"points": [v(4.49, -8.14) * mm, v(4.48, -8.17) * mm, v(4.46, -8.2) * mm, v(4.46, -8.2) * mm]});
            skFitSpline(sketch, "E251", {"points": [v(4.46, -8.2) * mm, v(4.45, -8.2) * mm, v(4.44, -8.2) * mm, v(4.44, -8.22) * mm]});
            skFitSpline(sketch, "E252", {"points": [v(4.44, -8.22) * mm, v(4.44, -8.25) * mm, v(4.3, -8.5) * mm, v(4.2, -8.63) * mm]});
            skFitSpline(sketch, "E253", {"points": [v(4.2, -8.63) * mm, v(4.17, -8.68) * mm, v(4.14, -8.73) * mm, v(4.14, -8.74) * mm]});
            skFitSpline(sketch, "E254", {"points": [v(4.14, -8.74) * mm, v(4.14, -8.74) * mm, v(4.12, -8.78) * mm, v(4.1, -8.81) * mm]});
            skFitSpline(sketch, "E255", {"points": [v(4.1, -8.81) * mm, v(4.06, -8.85) * mm, v(4.04, -8.88) * mm, v(4.03, -8.9) * mm]});
            skFitSpline(sketch, "E256", {"points": [v(4.03, -8.9) * mm, v(3.98, -8.96) * mm, v(3.8, -9.17) * mm, v(3.63, -9.35) * mm]});
            skFitSpline(sketch, "E257", {"points": [v(3.63, -9.35) * mm, v(3.6, -9.38) * mm, v(3.55, -9.44) * mm, v(3.52, -9.48) * mm]});
            skFitSpline(sketch, "E258", {"points": [v(3.52, -9.48) * mm, v(3.4, -9.62) * mm, v(3, -10.01) * mm, v(2.83, -10.16) * mm]});
            skFitSpline(sketch, "E259", {"points": [v(2.83, -10.16) * mm, v(2.73, -10.25) * mm, v(2.63, -10.33) * mm, v(2.62, -10.34) * mm]});
            skFitSpline(sketch, "E260", {"points": [v(2.62, -10.34) * mm, v(2.56, -10.39) * mm, v(2.32, -10.57) * mm, v(2.25, -10.62) * mm]});
            skFitSpline(sketch, "E261", {"points": [v(2.25, -10.62) * mm, v(2.21, -10.64) * mm, v(2.16, -10.68) * mm, v(2.14, -10.7) * mm]});
            skFitSpline(sketch, "E262", {"points": [v(2.14, -10.7) * mm, v(2.12, -10.7) * mm, v(2.06, -10.74) * mm, v(2.01, -10.76) * mm]});
            skFitSpline(sketch, "E263", {"points": [v(2.01, -10.76) * mm, v(1.96, -10.79) * mm, v(1.9, -10.82) * mm, v(1.87, -10.84) * mm]});
            skFitSpline(sketch, "E264", {"points": [v(1.87, -10.84) * mm, v(1.8, -10.9) * mm, v(1.2, -11.2) * mm, v(1.03, -11.26) * mm]});
            skFitSpline(sketch, "E265", {"points": [v(1.03, -11.26) * mm, v(0.97, -11.28) * mm, v(0.85, -11.32) * mm, v(0.76, -11.35) * mm]});
            skFitSpline(sketch, "E266", {"points": [v(0.76, -11.35) * mm, v(0.68, -11.38) * mm, v(0.57, -11.42) * mm, v(0.52, -11.43) * mm]});
            skFitSpline(sketch, "E267", {"points": [v(0.52, -11.43) * mm, v(0.27, -11.51) * mm, v(0.12, -11.55) * mm, v(0.07, -11.57) * mm]});
            skFitSpline(sketch, "E268", {"points": [v(0.07, -11.57) * mm, v(0.03, -11.58) * mm, v(-0.1, -11.61) * mm, v(-0.22, -11.64) * mm]});
            skFitSpline(sketch, "E269", {"points": [v(-0.22, -11.64) * mm, v(-0.5, -11.72) * mm, v(-0.92, -11.82) * mm, v(-1.08, -11.85) * mm]});
            skFitSpline(sketch, "E270", {"points": [v(-1.08, -11.85) * mm, v(-1.14, -11.87) * mm, v(-1.23, -11.89) * mm, v(-1.26, -11.9) * mm]});
            skFitSpline(sketch, "E271", {"points": [v(-1.26, -11.9) * mm, v(-1.3, -11.91) * mm, v(-1.39, -11.93) * mm, v(-1.46, -11.95) * mm]});
            skFitSpline(sketch, "E272", {"points": [v(-1.46, -11.95) * mm, v(-1.54, -11.96) * mm, v(-1.64, -11.98) * mm, v(-1.7, -12) * mm]});
            skFitSpline(sketch, "E273", {"points": [v(-1.7, -12) * mm, v(-1.75, -12) * mm, v(-1.89, -12.04) * mm, v(-2, -12.07) * mm]});
            skFitSpline(sketch, "E274", {"points": [v(-2, -12.07) * mm, v(-2.12, -12.1) * mm, v(-2.33, -12.14) * mm, v(-2.46, -12.17) * mm]});
            skFitSpline(sketch, "E275", {"points": [v(-2.46, -12.17) * mm, v(-2.6, -12.2) * mm, v(-2.77, -12.23) * mm, v(-2.85, -12.24) * mm]});
            skFitSpline(sketch, "E276", {"points": [v(-2.85, -12.24) * mm, v(-2.94, -12.25) * mm, v(-3.05, -12.27) * mm, v(-3.1, -12.28) * mm]});
            skFitSpline(sketch, "E277", {"points": [v(-3.1, -12.28) * mm, v(-3.2, -12.3) * mm, v(-3.22, -12.3) * mm, v(-3.41, -12.33) * mm]});
            skFitSpline(sketch, "E278", {"points": [v(-3.41, -12.33) * mm, v(-3.47, -12.34) * mm, v(-3.55, -12.35) * mm, v(-3.59, -12.36) * mm]});
            skFitSpline(sketch, "E279", {"points": [v(-3.59, -12.36) * mm, v(-3.63, -12.36) * mm, v(-3.74, -12.38) * mm, v(-3.84, -12.4) * mm]});
            skFitSpline(sketch, "E280", {"points": [v(-3.84, -12.4) * mm, v(-3.93, -12.4) * mm, v(-4.12, -12.44) * mm, v(-4.25, -12.47) * mm]});
            skFitSpline(sketch, "E281", {"points": [v(-4.48, -12.6) * mm, v(-4.47, -12.63) * mm, v(-4.46, -12.68) * mm, v(-4.46, -12.7) * mm]});
            skFitSpline(sketch, "E282", {"points": [v(-4.46, -12.7) * mm, v(-4.45, -12.74) * mm, v(-4.47, -12.75) * mm, v(-4.5, -12.72) * mm]});
            skFitSpline(sketch, "E283", {"points": [v(-4.33, -12.37) * mm, v(-4.24, -12.35) * mm, v(-4.1, -12.33) * mm, v(-4.03, -12.31) * mm]});
            skFitSpline(sketch, "E284", {"points": [v(-4.03, -12.31) * mm, v(-3.79, -12.27) * mm, v(-3.61, -12.24) * mm, v(-3.5, -12.23) * mm]});
            skFitSpline(sketch, "E285", {"points": [v(-3.5, -12.23) * mm, v(-3.2, -12.2) * mm, v(-2.48, -12.07) * mm, v(-2.1, -11.98) * mm]});
            skFitSpline(sketch, "E286", {"points": [v(-2.1, -11.98) * mm, v(-1.87, -11.93) * mm, v(-1.48, -11.84) * mm, v(-1.36, -11.82) * mm]});
            skFitSpline(sketch, "E287", {"points": [v(-1.36, -11.82) * mm, v(-1.17, -11.77) * mm, v(-0.94, -11.72) * mm, v(-0.91, -11.7) * mm]});
            skFitSpline(sketch, "E288", {"points": [v(-0.91, -11.7) * mm, v(-0.9, -11.69) * mm, v(-0.87, -11.68) * mm, v(-0.85, -11.68) * mm]});
            skFitSpline(sketch, "E289", {"points": [v(-0.85, -11.68) * mm, v(-0.81, -11.68) * mm, v(-0.4, -11.6) * mm, v(-0.35, -11.57) * mm]});
            skFitSpline(sketch, "E290", {"points": [v(-0.35, -11.57) * mm, v(-0.33, -11.56) * mm, v(-0.28, -11.55) * mm, v(-0.26, -11.55) * mm]});
            skFitSpline(sketch, "E291", {"points": [v(-0.26, -11.55) * mm, v(-0.2, -11.54) * mm, v(-0.1, -11.51) * mm, v(0, -11.48) * mm]});
            skFitSpline(sketch, "E292", {"points": [v(0, -11.48) * mm, v(0.03, -11.47) * mm, v(0.18, -11.43) * mm, v(0.32, -11.4) * mm]});
            skFitSpline(sketch, "E293", {"points": [v(0.32, -11.4) * mm, v(0.45, -11.36) * mm, v(0.57, -11.32) * mm, v(0.57, -11.31) * mm]});
            skFitSpline(sketch, "E294", {"points": [v(0.57, -11.31) * mm, v(0.58, -11.3) * mm, v(0.62, -11.3) * mm, v(0.67, -11.28) * mm]});
            skFitSpline(sketch, "E295", {"points": [v(0.67, -11.28) * mm, v(0.83, -11.23) * mm, v(1.27, -11.06) * mm, v(1.3, -11.03) * mm]});
            skFitSpline(sketch, "E296", {"points": [v(1.3, -11.03) * mm, v(1.3, -11.02) * mm, v(1.32, -11.01) * mm, v(1.33, -11.01) * mm]});
            skFitSpline(sketch, "E297", {"points": [v(1.33, -11.01) * mm, v(1.35, -11.01) * mm, v(1.4, -10.98) * mm, v(1.61, -10.87) * mm]});
            skFitSpline(sketch, "E298", {"points": [v(1.61, -10.87) * mm, v(1.63, -10.86) * mm, v(1.66, -10.85) * mm, v(1.67, -10.85) * mm]});
            skFitSpline(sketch, "E299", {"points": [v(1.67, -10.85) * mm, v(1.68, -10.85) * mm, v(1.7, -10.84) * mm, v(1.7, -10.84) * mm]});
            skFitSpline(sketch, "E300", {"points": [v(1.7, -10.84) * mm, v(1.7, -10.83) * mm, v(1.72, -10.8) * mm, v(1.75, -10.8) * mm]});
            skFitSpline(sketch, "E301", {"points": [v(1.75, -10.8) * mm, v(1.78, -10.78) * mm, v(1.83, -10.75) * mm, v(1.84, -10.74) * mm]});
            skFitSpline(sketch, "E302", {"points": [v(1.84, -10.74) * mm, v(1.86, -10.72) * mm, v(1.93, -10.68) * mm, v(2, -10.64) * mm]});
            skFitSpline(sketch, "E303", {"points": [v(2, -10.64) * mm, v(2.17, -10.56) * mm, v(2.31, -10.46) * mm, v(2.42, -10.37) * mm]});
            skFitSpline(sketch, "E304", {"points": [v(2.42, -10.37) * mm, v(2.44, -10.34) * mm, v(2.52, -10.28) * mm, v(2.58, -10.23) * mm]});
            skFitSpline(sketch, "E305", {"points": [v(2.58, -10.23) * mm, v(3.03, -9.86) * mm, v(3.4, -9.47) * mm, v(3.92, -8.84) * mm]});
            skFitSpline(sketch, "E306", {"points": [v(3.92, -8.84) * mm, v(4, -8.75) * mm, v(4.14, -8.55) * mm, v(4.2, -8.43) * mm]});
            skFitSpline(sketch, "E307", {"points": [v(4.2, -8.43) * mm, v(4.23, -8.38) * mm, v(4.28, -8.3) * mm, v(4.31, -8.25) * mm]});
            skFitSpline(sketch, "E308", {"points": [v(4.31, -8.25) * mm, v(4.36, -8.16) * mm, v(4.39, -8.1) * mm, v(4.5, -7.87) * mm]});
            skFitSpline(sketch, "E309", {"points": [v(4.5, -7.87) * mm, v(4.6, -7.63) * mm, v(4.62, -7.61) * mm, v(4.63, -7.55) * mm]});
            skFitSpline(sketch, "E310", {"points": [v(4.63, -7.55) * mm, v(4.65, -7.51) * mm, v(4.66, -7.47) * mm, v(4.68, -7.44) * mm]});
            skFitSpline(sketch, "E311", {"points": [v(4.68, -7.44) * mm, v(4.7, -7.38) * mm, v(4.8, -7) * mm, v(4.84, -6.83) * mm]});
            skFitSpline(sketch, "E312", {"points": [v(4.84, -6.83) * mm, v(4.9, -6.5) * mm, v(4.9, -6.26) * mm, v(4.9, -5.97) * mm]});
            skFitSpline(sketch, "E313", {"points": [v(4.9, -5.97) * mm, v(4.9, -5.82) * mm, v(4.88, -5.66) * mm, v(4.87, -5.61) * mm]});
            skFitSpline(sketch, "E314", {"points": [v(4.87, -5.61) * mm, v(4.87, -5.57) * mm, v(4.86, -5.5) * mm, v(4.86, -5.45) * mm]});
            skFitSpline(sketch, "E315", {"points": [v(4.86, -5.45) * mm, v(4.86, -5.33) * mm, v(4.73, -4.73) * mm, v(4.67, -4.6) * mm]});
            skFitSpline(sketch, "E316", {"points": [v(4.67, -4.6) * mm, v(4.66, -4.57) * mm, v(4.65, -4.54) * mm, v(4.66, -4.53) * mm]});
            skFitSpline(sketch, "E317", {"points": [v(4.66, -4.53) * mm, v(4.66, -4.52) * mm, v(4.66, -4.52) * mm, v(4.65, -4.52) * mm]});
            skFitSpline(sketch, "E318", {"points": [v(4.65, -4.52) * mm, v(4.64, -4.52) * mm, v(4.63, -4.48) * mm, v(4.63, -4.44) * mm]});
            skFitSpline(sketch, "E319", {"points": [v(4.63, -4.44) * mm, v(4.62, -4.4) * mm, v(4.6, -4.36) * mm, v(4.6, -4.36) * mm]});
            skFitSpline(sketch, "E320", {"points": [v(4.6, -4.36) * mm, v(4.6, -4.36) * mm, v(4.59, -4.34) * mm, v(4.6, -4.33) * mm]});
            skFitSpline(sketch, "E321", {"points": [v(4.6, -4.33) * mm, v(4.6, -4.32) * mm, v(4.6, -4.29) * mm, v(4.58, -4.27) * mm]});
            skFitSpline(sketch, "E322", {"points": [v(4.58, -4.27) * mm, v(4.56, -4.25) * mm, v(4.56, -4.22) * mm, v(4.56, -4.2) * mm]});
            skFitSpline(sketch, "E323", {"points": [v(4.56, -4.2) * mm, v(4.57, -4.18) * mm, v(4.57, -4.16) * mm, v(4.56, -4.16) * mm]});
            skFitSpline(sketch, "E324", {"points": [v(4.56, -4.16) * mm, v(4.55, -4.16) * mm, v(4.53, -4.13) * mm, v(4.52, -4.08) * mm]});
            skFitSpline(sketch, "E325", {"points": [v(4.52, -4.08) * mm, v(4.48, -3.98) * mm, v(4.45, -3.9) * mm, v(4.4, -3.82) * mm]});
            skFitSpline(sketch, "E326", {"points": [v(4.4, -3.82) * mm, v(4.4, -3.79) * mm, v(4.38, -3.74) * mm, v(4.38, -3.73) * mm]});
            skFitSpline(sketch, "E327", {"points": [v(4.38, -3.73) * mm, v(4.38, -3.71) * mm, v(4.37, -3.7) * mm, v(4.36, -3.7) * mm]});
            skFitSpline(sketch, "E328", {"points": [v(4.36, -3.7) * mm, v(4.35, -3.7) * mm, v(4.34, -3.68) * mm, v(4.34, -3.66) * mm]});
            skFitSpline(sketch, "E329", {"points": [v(4.34, -3.66) * mm, v(4.33, -3.6) * mm, v(4.31, -3.56) * mm, v(4.3, -3.56) * mm]});
            skFitSpline(sketch, "E330", {"points": [v(4.3, -3.56) * mm, v(4.3, -3.56) * mm, v(4.28, -3.52) * mm, v(4.27, -3.48) * mm]});
            skFitSpline(sketch, "E331", {"points": [v(4.27, -3.48) * mm, v(4.26, -3.44) * mm, v(4.24, -3.41) * mm, v(4.24, -3.41) * mm]});
            skFitSpline(sketch, "E332", {"points": [v(4.24, -3.41) * mm, v(4.23, -3.41) * mm, v(4.22, -3.39) * mm, v(4.2, -3.35) * mm]});
            skFitSpline(sketch, "E333", {"points": [v(4.2, -3.35) * mm, v(4.17, -3.24) * mm, v(4.13, -3.17) * mm, v(4.12, -3.17) * mm]});
            skFitSpline(sketch, "E334", {"points": [v(4.12, -3.17) * mm, v(4.11, -3.17) * mm, v(4.1, -3.16) * mm, v(4.1, -3.16) * mm]});
            skFitSpline(sketch, "E335", {"points": [v(4.1, -3.16) * mm, v(4.1, -3.13) * mm, v(4.03, -2.97) * mm, v(3.99, -2.9) * mm]});
            skFitSpline(sketch, "E336", {"points": [v(3.99, -2.9) * mm, v(3.97, -2.87) * mm, v(3.94, -2.8) * mm, v(3.92, -2.76) * mm]});
            skFitSpline(sketch, "E337", {"points": [v(3.92, -2.76) * mm, v(3.9, -2.71) * mm, v(3.89, -2.68) * mm, v(3.88, -2.68) * mm]});
            skFitSpline(sketch, "E338", {"points": [v(3.88, -2.68) * mm, v(3.87, -2.68) * mm, v(3.87, -2.67) * mm, v(3.87, -2.65) * mm]});
            skFitSpline(sketch, "E339", {"points": [v(3.87, -2.65) * mm, v(3.87, -2.64) * mm, v(3.86, -2.62) * mm, v(3.85, -2.6) * mm]});
            skFitSpline(sketch, "E340", {"points": [v(3.85, -2.6) * mm, v(3.84, -2.6) * mm, v(3.8, -2.55) * mm, v(3.78, -2.5) * mm]});
            skFitSpline(sketch, "E341", {"points": [v(3.78, -2.5) * mm, v(3.75, -2.44) * mm, v(3.72, -2.38) * mm, v(3.7, -2.37) * mm]});
            skFitSpline(sketch, "E342", {"points": [v(3.7, -2.37) * mm, v(3.7, -2.36) * mm, v(3.69, -2.33) * mm, v(3.68, -2.32) * mm]});
            skFitSpline(sketch, "E343", {"points": [v(3.68, -2.32) * mm, v(3.68, -2.3) * mm, v(3.6, -2.18) * mm, v(3.5, -2) * mm]});
            skFitSpline(sketch, "E344", {"points": [v(3.5, -2) * mm, v(3.46, -1.93) * mm, v(3.41, -1.85) * mm, v(3.34, -1.72) * mm]});
            skFitSpline(sketch, "E345", {"points": [v(3.34, -1.72) * mm, v(3.31, -1.66) * mm, v(3.26, -1.57) * mm, v(3.23, -1.5) * mm]});
            skFitSpline(sketch, "E346", {"points": [v(3.23, -1.5) * mm, v(3.17, -1.41) * mm, v(3.1, -1.26) * mm, v(3.06, -1.17) * mm]});
            skFitSpline(sketch, "E347", {"points": [v(3.06, -1.17) * mm, v(3.05, -1.15) * mm, v(3.03, -1.12) * mm, v(3.02, -1.1) * mm]});
            skFitSpline(sketch, "E348", {"points": [v(3.02, -1.1) * mm, v(3, -1.1) * mm, v(2.98, -1.06) * mm, v(2.98, -1.04) * mm]});
            skFitSpline(sketch, "E349", {"points": [v(2.98, -1.04) * mm, v(2.97, -1.01) * mm, v(2.96, -1) * mm, v(2.95, -1) * mm]});
            skFitSpline(sketch, "E350", {"points": [v(2.95, -1) * mm, v(2.95, -1) * mm, v(2.94, -0.99) * mm, v(2.94, -0.97) * mm]});
            skFitSpline(sketch, "E351", {"points": [v(2.94, -0.97) * mm, v(2.94, -0.96) * mm, v(2.91, -0.91) * mm, v(2.88, -0.86) * mm]});
            skFitSpline(sketch, "E352", {"points": [v(2.88, -0.86) * mm, v(2.85, -0.82) * mm, v(2.83, -0.77) * mm, v(2.83, -0.76) * mm]});
            skFitSpline(sketch, "E353", {"points": [v(2.83, -0.76) * mm, v(2.83, -0.74) * mm, v(2.81, -0.72) * mm, v(2.8, -0.7) * mm]});
            skFitSpline(sketch, "E354", {"points": [v(2.8, -0.7) * mm, v(2.78, -0.68) * mm, v(2.76, -0.66) * mm, v(2.76, -0.64) * mm]});
            skFitSpline(sketch, "E355", {"points": [v(2.76, -0.64) * mm, v(2.75, -0.63) * mm, v(2.73, -0.6) * mm, v(2.71, -0.56) * mm]});
            skFitSpline(sketch, "E356", {"points": [v(2.71, -0.56) * mm, v(2.65, -0.46) * mm, v(2.57, -0.3) * mm, v(2.57, -0.28) * mm]});
            skFitSpline(sketch, "E357", {"points": [v(2.57, -0.28) * mm, v(2.57, -0.27) * mm, v(2.56, -0.26) * mm, v(2.56, -0.26) * mm]});
            skFitSpline(sketch, "E358", {"points": [v(2.56, -0.26) * mm, v(2.54, -0.26) * mm, v(2.45, -0.13) * mm, v(2.4, -0.02) * mm]});
            skFitSpline(sketch, "E359", {"points": [v(2.4, -0.02) * mm, v(2.38, 0.02) * mm, v(2.34, 0.1) * mm, v(2.3, 0.14) * mm]});
            skFitSpline(sketch, "E360", {"points": [v(2.3, 0.14) * mm, v(2.28, 0.19) * mm, v(2.25, 0.24) * mm, v(2.25, 0.26) * mm]});
            skFitSpline(sketch, "E361", {"points": [v(2.25, 0.26) * mm, v(2.25, 0.27) * mm, v(2.24, 0.28) * mm, v(2.24, 0.28) * mm]});
            skFitSpline(sketch, "E362", {"points": [v(2.24, 0.28) * mm, v(2.23, 0.28) * mm, v(2.19, 0.35) * mm, v(2.14, 0.44) * mm]});
            skFitSpline(sketch, "E363", {"points": [v(2.14, 0.44) * mm, v(2.03, 0.65) * mm, v(2, 0.7) * mm, v(2, 0.72) * mm]});
            skFitSpline(sketch, "E364", {"points": [v(2, 0.72) * mm, v(1.99, 0.72) * mm, v(1.97, 0.75) * mm, v(1.95, 0.79) * mm]});
            skFitSpline(sketch, "E365", {"points": [v(1.95, 0.79) * mm, v(1.94, 0.82) * mm, v(1.92, 0.85) * mm, v(1.91, 0.86) * mm]});
            skFitSpline(sketch, "E366", {"points": [v(1.91, 0.86) * mm, v(1.9, 0.86) * mm, v(1.9, 0.88) * mm, v(1.9, 0.9) * mm]});
            skFitSpline(sketch, "E367", {"points": [v(1.9, 0.9) * mm, v(1.88, 0.93) * mm, v(1.87, 0.96) * mm, v(1.86, 0.97) * mm]});
            skFitSpline(sketch, "E368", {"points": [v(1.86, 0.97) * mm, v(1.85, 0.98) * mm, v(1.82, 1.04) * mm, v(1.79, 1.1) * mm]});
            skFitSpline(sketch, "E369", {"points": [v(1.79, 1.1) * mm, v(1.76, 1.14) * mm, v(1.73, 1.2) * mm, v(1.72, 1.2) * mm]});
            skFitSpline(sketch, "E370", {"points": [v(1.72, 1.2) * mm, v(1.71, 1.22) * mm, v(1.7, 1.23) * mm, v(1.71, 1.23) * mm]});
            skFitSpline(sketch, "E371", {"points": [v(1.71, 1.23) * mm, v(1.72, 1.23) * mm, v(1.71, 1.25) * mm, v(1.7, 1.27) * mm]});
            skFitSpline(sketch, "E372", {"points": [v(1.7, 1.27) * mm, v(1.68, 1.3) * mm, v(1.65, 1.35) * mm, v(1.63, 1.39) * mm]});
            skFitSpline(sketch, "E373", {"points": [v(1.63, 1.39) * mm, v(1.53, 1.6) * mm, v(1.49, 1.68) * mm, v(1.48, 1.69) * mm]});
            skFitSpline(sketch, "E374", {"points": [v(1.48, 1.69) * mm, v(1.47, 1.7) * mm, v(1.47, 1.7) * mm, v(1.47, 1.72) * mm]});
            skFitSpline(sketch, "E375", {"points": [v(1.47, 1.72) * mm, v(1.47, 1.74) * mm, v(1.37, 1.95) * mm, v(1.36, 1.96) * mm]});
            skFitSpline(sketch, "E376", {"points": [v(1.36, 1.96) * mm, v(1.35, 1.97) * mm, v(1.32, 2.04) * mm, v(1.28, 2.11) * mm]});
            skFitSpline(sketch, "E377", {"points": [v(1.28, 2.11) * mm, v(1.24, 2.2) * mm, v(1.2, 2.27) * mm, v(1.2, 2.28) * mm]});
            skFitSpline(sketch, "E378", {"points": [v(1.2, 2.28) * mm, v(1.19, 2.3) * mm, v(1.17, 2.32) * mm, v(1.16, 2.34) * mm]});
            skFitSpline(sketch, "E379", {"points": [v(1.16, 2.34) * mm, v(1.16, 2.36) * mm, v(1.14, 2.38) * mm, v(1.13, 2.39) * mm]});
            skFitSpline(sketch, "E380", {"points": [v(1.13, 2.39) * mm, v(1.12, 2.4) * mm, v(1.12, 2.41) * mm, v(1.12, 2.43) * mm]});
            skFitSpline(sketch, "E381", {"points": [v(1.12, 2.43) * mm, v(1.12, 2.44) * mm, v(1.1, 2.48) * mm, v(1.08, 2.51) * mm]});
            skFitSpline(sketch, "E382", {"points": [v(1.08, 2.51) * mm, v(1.07, 2.54) * mm, v(1.04, 2.6) * mm, v(1.02, 2.65) * mm]});
            skFitSpline(sketch, "E383", {"points": [v(1.02, 2.65) * mm, v(1, 2.7) * mm, v(0.98, 2.76) * mm, v(0.97, 2.78) * mm]});
            skFitSpline(sketch, "E384", {"points": [v(0.97, 2.78) * mm, v(0.96, 2.8) * mm, v(0.94, 2.83) * mm, v(0.94, 2.85) * mm]});
            skFitSpline(sketch, "E385", {"points": [v(0.94, 2.85) * mm, v(0.93, 2.87) * mm, v(0.91, 2.91) * mm, v(0.9, 2.93) * mm]});
            skFitSpline(sketch, "E386", {"points": [v(0.9, 2.93) * mm, v(0.9, 2.96) * mm, v(0.88, 3) * mm, v(0.87, 3.01) * mm]});
            skFitSpline(sketch, "E387", {"points": [v(0.87, 3.01) * mm, v(0.87, 3.03) * mm, v(0.85, 3.07) * mm, v(0.84, 3.09) * mm]});
            skFitSpline(sketch, "E388", {"points": [v(0.84, 3.09) * mm, v(0.84, 3.1) * mm, v(0.81, 3.16) * mm, v(0.8, 3.2) * mm]});
            skFitSpline(sketch, "E389", {"points": [v(0.8, 3.2) * mm, v(0.78, 3.25) * mm, v(0.75, 3.31) * mm, v(0.73, 3.34) * mm]});
            skFitSpline(sketch, "E390", {"points": [v(0.73, 3.34) * mm, v(0.71, 3.38) * mm, v(0.7, 3.41) * mm, v(0.7, 3.42) * mm]});
            skFitSpline(sketch, "E391", {"points": [v(0.7, 3.42) * mm, v(0.7, 3.43) * mm, v(0.68, 3.47) * mm, v(0.66, 3.52) * mm]});
            skFitSpline(sketch, "E392", {"points": [v(0.66, 3.52) * mm, v(0.64, 3.56) * mm, v(0.62, 3.62) * mm, v(0.62, 3.65) * mm]});
            skFitSpline(sketch, "E393", {"points": [v(0.62, 3.65) * mm, v(0.61, 3.67) * mm, v(0.6, 3.7) * mm, v(0.6, 3.7) * mm]});
            skFitSpline(sketch, "E394", {"points": [v(0.6, 3.7) * mm, v(0.58, 3.72) * mm, v(0.57, 3.73) * mm, v(0.57, 3.74) * mm]});
            skFitSpline(sketch, "E395", {"points": [v(0.57, 3.74) * mm, v(0.57, 3.75) * mm, v(0.56, 3.78) * mm, v(0.54, 3.82) * mm]});
            skFitSpline(sketch, "E396", {"points": [v(0.54, 3.82) * mm, v(0.52, 3.85) * mm, v(0.52, 3.88) * mm, v(0.53, 3.87) * mm]});
            skFitSpline(sketch, "E397", {"points": [v(0.53, 3.87) * mm, v(0.53, 3.87) * mm, v(0.53, 3.88) * mm, v(0.52, 3.9) * mm]});
            skFitSpline(sketch, "E398", {"points": [v(0.52, 3.9) * mm, v(0.5, 3.92) * mm, v(0.5, 3.93) * mm, v(0.49, 3.93) * mm]});
            skFitSpline(sketch, "E399", {"points": [v(0.49, 3.93) * mm, v(0.48, 3.93) * mm, v(0.48, 3.95) * mm, v(0.48, 3.97) * mm]});
            skFitSpline(sketch, "E400", {"points": [v(0.48, 3.97) * mm, v(0.48, 4) * mm, v(0.47, 4.01) * mm, v(0.46, 4.02) * mm]});
            skFitSpline(sketch, "E401", {"points": [v(0.46, 4.02) * mm, v(0.45, 4.02) * mm, v(0.44, 4.05) * mm, v(0.44, 4.08) * mm]});
            skFitSpline(sketch, "E402", {"points": [v(0.44, 4.08) * mm, v(0.43, 4.1) * mm, v(0.42, 4.15) * mm, v(0.4, 4.17) * mm]});
            skFitSpline(sketch, "E403", {"points": [v(0.4, 4.17) * mm, v(0.4, 4.2) * mm, v(0.38, 4.24) * mm, v(0.36, 4.28) * mm]});
            skFitSpline(sketch, "E404", {"points": [v(0.36, 4.28) * mm, v(0.35, 4.32) * mm, v(0.34, 4.36) * mm, v(0.33, 4.37) * mm]});
            skFitSpline(sketch, "E405", {"points": [v(0.33, 4.37) * mm, v(0.32, 4.38) * mm, v(0.32, 4.4) * mm, v(0.32, 4.42) * mm]});
            skFitSpline(sketch, "E406", {"points": [v(0.32, 4.42) * mm, v(0.32, 4.43) * mm, v(0.3, 4.47) * mm, v(0.3, 4.5) * mm]});
            skFitSpline(sketch, "E407", {"points": [v(0.3, 4.5) * mm, v(0.27, 4.55) * mm, v(0.22, 4.69) * mm, v(0.18, 4.83) * mm]});
            skFitSpline(sketch, "E408", {"points": [v(0.18, 4.83) * mm, v(0.17, 4.86) * mm, v(0.15, 4.9) * mm, v(0.14, 4.9) * mm]});
            skFitSpline(sketch, "E409", {"points": [v(0.14, 4.9) * mm, v(0.12, 4.91) * mm, v(0.02, 4.76) * mm, v(-0.18, 4.4) * mm]});
            skFitSpline(sketch, "E410", {"points": [v(-0.18, 4.4) * mm, v(-0.19, 4.37) * mm, v(-0.23, 4.3) * mm, v(-0.26, 4.25) * mm]});
            skFitSpline(sketch, "E411", {"points": [v(-0.26, 4.25) * mm, v(-0.3, 4.2) * mm, v(-0.35, 4.11) * mm, v(-0.37, 4.07) * mm]});
            skFitSpline(sketch, "E412", {"points": [v(-0.37, 4.07) * mm, v(-0.4, 4.02) * mm, v(-0.45, 3.93) * mm, v(-0.48, 3.87) * mm]});
            skFitSpline(sketch, "E413", {"points": [v(-0.48, 3.87) * mm, v(-0.52, 3.8) * mm, v(-0.6, 3.66) * mm, v(-0.66, 3.55) * mm]});
            skFitSpline(sketch, "E414", {"points": [v(-0.66, 3.55) * mm, v(-0.73, 3.44) * mm, v(-0.83, 3.25) * mm, v(-0.9, 3.13) * mm]});
            skFitSpline(sketch, "E415", {"points": [v(-0.9, 3.13) * mm, v(-0.96, 3.01) * mm, v(-1.02, 2.9) * mm, v(-1.04, 2.87) * mm]});
            skFitSpline(sketch, "E416", {"points": [v(-1.04, 2.87) * mm, v(-1.07, 2.82) * mm, v(-1.38, 2.19) * mm, v(-1.38, 2.17) * mm]});
            skFitSpline(sketch, "E417", {"points": [v(-1.38, 2.17) * mm, v(-1.38, 2.17) * mm, v(-1.41, 2.1) * mm, v(-1.45, 2.02) * mm]});
            skFitSpline(sketch, "E418", {"points": [v(-1.45, 2.02) * mm, v(-1.5, 1.94) * mm, v(-1.56, 1.8) * mm, v(-1.6, 1.7) * mm]});
            skFitSpline(sketch, "E419", {"points": [v(-1.6, 1.7) * mm, v(-1.64, 1.61) * mm, v(-1.7, 1.48) * mm, v(-1.73, 1.42) * mm]});
            skFitSpline(sketch, "E420", {"points": [v(-1.73, 1.42) * mm, v(-1.77, 1.35) * mm, v(-1.83, 1.2) * mm, v(-1.89, 1.1) * mm]});
            skFitSpline(sketch, "E421", {"points": [v(-1.89, 1.1) * mm, v(-1.94, 0.98) * mm, v(-2, 0.82) * mm, v(-2.05, 0.74) * mm]});
            skFitSpline(sketch, "E422", {"points": [v(-2.05, 0.74) * mm, v(-2.08, 0.66) * mm, v(-2.17, 0.47) * mm, v(-2.23, 0.32) * mm]});
            skFitSpline(sketch, "E423", {"points": [v(-2.23, 0.32) * mm, v(-2.3, 0.17) * mm, v(-2.36, 0.02) * mm, v(-2.38, -0.03) * mm]});
            skFitSpline(sketch, "E424", {"points": [v(-2.38, -0.03) * mm, v(-2.4, -0.07) * mm, v(-2.44, -0.17) * mm, v(-2.48, -0.25) * mm]});
            skFitSpline(sketch, "E425", {"points": [v(-2.48, -0.25) * mm, v(-2.5, -0.33) * mm, v(-2.55, -0.42) * mm, v(-2.56, -0.45) * mm]});
            skFitSpline(sketch, "E426", {"points": [v(-2.56, -0.45) * mm, v(-2.6, -0.53) * mm, v(-2.62, -0.58) * mm, v(-2.67, -0.72) * mm]});
            skFitSpline(sketch, "E427", {"points": [v(-2.67, -0.72) * mm, v(-2.74, -0.9) * mm, v(-2.78, -0.99) * mm, v(-2.8, -1.02) * mm]});
            skFitSpline(sketch, "E428", {"points": [v(-2.8, -1.02) * mm, v(-2.8, -1.03) * mm, v(-2.8, -1.05) * mm, v(-2.8, -1.06) * mm]});
            skFitSpline(sketch, "E429", {"points": [v(-2.8, -1.06) * mm, v(-2.8, -1.08) * mm, v(-2.94, -1.47) * mm, v(-2.97, -1.55) * mm]});
            skFitSpline(sketch, "E430", {"points": [v(-2.97, -1.55) * mm, v(-2.98, -1.58) * mm, v(-3, -1.64) * mm, v(-3.03, -1.7) * mm]});
            skFitSpline(sketch, "E431", {"points": [v(-3.03, -1.7) * mm, v(-3.04, -1.76) * mm, v(-3.07, -1.84) * mm, v(-3.1, -1.9) * mm]});
            skFitSpline(sketch, "E432", {"points": [v(-3.1, -1.9) * mm, v(-3.11, -1.94) * mm, v(-3.14, -2.02) * mm, v(-3.16, -2.08) * mm]});
            skFitSpline(sketch, "E433", {"points": [v(-3.16, -2.08) * mm, v(-3.17, -2.13) * mm, v(-3.22, -2.28) * mm, v(-3.27, -2.4) * mm]});
            skFitSpline(sketch, "E434", {"points": [v(-3.27, -2.4) * mm, v(-3.38, -2.71) * mm, v(-3.41, -2.8) * mm, v(-3.44, -2.93) * mm]});
            skFitSpline(sketch, "E435", {"points": [v(-3.44, -2.93) * mm, v(-3.47, -3.03) * mm, v(-3.52, -3.16) * mm, v(-3.54, -3.23) * mm]});
            skFitSpline(sketch, "E436", {"points": [v(-3.54, -3.23) * mm, v(-3.55, -3.26) * mm, v(-3.6, -3.43) * mm, v(-3.63, -3.55) * mm]});
            skFitSpline(sketch, "E437", {"points": [v(-3.63, -3.55) * mm, v(-3.64, -3.57) * mm, v(-3.65, -3.59) * mm, v(-3.65, -3.59) * mm]});
            skFitSpline(sketch, "E438", {"points": [v(-3.65, -3.59) * mm, v(-3.66, -3.59) * mm, v(-3.66, -3.6) * mm, v(-3.66, -3.62) * mm]});
            skFitSpline(sketch, "E439", {"points": [v(-3.66, -3.62) * mm, v(-3.67, -3.66) * mm, v(-3.72, -3.87) * mm, v(-3.75, -3.93) * mm]});
            skFitSpline(sketch, "E440", {"points": [v(-3.75, -3.93) * mm, v(-3.75, -3.95) * mm, v(-3.77, -4) * mm, v(-3.78, -4.04) * mm]});
            skFitSpline(sketch, "E441", {"points": [v(-3.78, -4.04) * mm, v(-3.79, -4.08) * mm, v(-3.82, -4.18) * mm, v(-3.84, -4.26) * mm]});
            skFitSpline(sketch, "E442", {"points": [v(-3.84, -4.26) * mm, v(-3.86, -4.34) * mm, v(-3.9, -4.46) * mm, v(-3.9, -4.5) * mm]});
            skFitSpline(sketch, "E443", {"points": [v(-3.9, -4.5) * mm, v(-3.92, -4.56) * mm, v(-3.93, -4.62) * mm, v(-3.94, -4.64) * mm]});
            skFitSpline(sketch, "E444", {"points": [v(-3.94, -4.64) * mm, v(-3.95, -4.65) * mm, v(-3.96, -4.69) * mm, v(-3.96, -4.72) * mm]});
            skFitSpline(sketch, "E445", {"points": [v(-3.96, -4.72) * mm, v(-3.97, -4.74) * mm, v(-4, -4.86) * mm, v(-4.02, -4.99) * mm]});
            skFitSpline(sketch, "E446", {"points": [v(-4.02, -4.99) * mm, v(-4.12, -5.46) * mm, v(-4.23, -5.97) * mm, v(-4.25, -6.1) * mm]});
            skFitSpline(sketch, "E447", {"points": [v(-4.25, -6.1) * mm, v(-4.27, -6.16) * mm, v(-4.28, -6.23) * mm, v(-4.29, -6.24) * mm]});
            skFitSpline(sketch, "E448", {"points": [v(-4.29, -6.24) * mm, v(-4.3, -6.26) * mm, v(-4.3, -6.28) * mm, v(-4.3, -6.28) * mm]});
            skFitSpline(sketch, "E449", {"points": [v(-4.3, -6.28) * mm, v(-4.3, -6.31) * mm, v(-4.33, -6.43) * mm, v(-4.36, -6.57) * mm]});
            skFitSpline(sketch, "E450", {"points": [v(-4.36, -6.57) * mm, v(-4.37, -6.65) * mm, v(-4.4, -6.82) * mm, v(-4.42, -6.95) * mm]});
            skFitSpline(sketch, "E451", {"points": [v(-4.42, -6.95) * mm, v(-4.44, -7.08) * mm, v(-4.46, -7.2) * mm, v(-4.47, -7.21) * mm]});
            skFitSpline(sketch, "E452", {"points": [v(-4.47, -7.21) * mm, v(-4.48, -7.25) * mm, v(-4.54, -7.73) * mm, v(-4.56, -7.9) * mm]});
            skFitSpline(sketch, "E453", {"points": [v(-4.56, -7.9) * mm, v(-4.56, -7.96) * mm, v(-4.57, -8.08) * mm, v(-4.58, -8.16) * mm]});
            skFitSpline(sketch, "E454", {"points": [v(-4.58, -8.16) * mm, v(-4.63, -8.66) * mm, v(-4.65, -8.94) * mm, v(-4.67, -9.36) * mm]});
            skFitSpline(sketch, "E455", {"points": [v(-4.67, -9.36) * mm, v(-4.67, -9.47) * mm, v(-4.68, -9.64) * mm, v(-4.68, -9.72) * mm]});
            skFitSpline(sketch, "E456", {"points": [v(-4.68, -9.72) * mm, v(-4.7, -10.06) * mm, v(-4.7, -11.05) * mm, v(-4.67, -11.3) * mm]});
            skFitSpline(sketch, "E457", {"points": [v(-4.67, -11.3) * mm, v(-4.65, -11.42) * mm, v(-4.64, -11.63) * mm, v(-4.63, -11.75) * mm]});
            skFitSpline(sketch, "E458", {"points": [v(-4.63, -11.75) * mm, v(-4.62, -11.88) * mm, v(-4.6, -12.04) * mm, v(-4.6, -12.1) * mm]});
            skFitSpline(sketch, "E459", {"points": [v(-4.6, -12.1) * mm, v(-4.58, -12.24) * mm, v(-4.53, -12.4) * mm, v(-4.52, -12.4) * mm]});
            skFitSpline(sketch, "E460", {"points": [v(-4.52, -12.4) * mm, v(-4.51, -12.4) * mm, v(-4.43, -12.39) * mm, v(-4.33, -12.37) * mm]});
            skLineSegment(sketch, "E461.bottom", {"start": v(7.18, 14.04) * mm, "end": v(-7.08, 14.04) * mm});
            skLineSegment(sketch, "E461.top", {"start": v(7.18, -13.76) * mm, "end": v(-7.08, -13.76) * mm});
            skLineSegment(sketch, "E461.left", {"start": v(7.18, 14.04) * mm, "end": v(7.18, -13.76) * mm});
            skLineSegment(sketch, "E461.right", {"start": v(-7.08, 14.04) * mm, "end": v(-7.08, -13.76) * mm});
            skSolve(sketch);
        }
        {
            var Q0;
            Q0 = qSketchRegion(id + "F2", true);
            extrude(context, id + "F3", {"entities" : qUnion([Q0]), "depth" : 6.35 * mm, "offsetDistance" : 25.4 * mm});
        }
        {
            var Q0;
            Q0=makeQuery(id+"F3.opExtrude","SWEPT_BODY",BODY,{"disambiguationData":[OSD([sQuery(id+"F2.wireOp",EDGE,"E4"),sQuery(id+"F2.wireOp",EDGE,"E7"),sQuery(id+"F2.wireOp",EDGE,"E8"),sQuery(id+"F2.wireOp",EDGE,"E9"),sQuery(id+"F2.wireOp",EDGE,"E10"),sQuery(id+"F2.wireOp",EDGE,"E11"),sQuery(id+"F2.wireOp",EDGE,"E12"),sQuery(id+"F2.wireOp",EDGE,"E13"),sQuery(id+"F2.wireOp",EDGE,"E14"),sQuery(id+"F2.wireOp",EDGE,"E15"),sQuery(id+"F2.wireOp",EDGE,"E16"),sQuery(id+"F2.wireOp",EDGE,"E17"),sQuery(id+"F2.wireOp",EDGE,"E18"),sQuery(id+"F2.wireOp",EDGE,"E19"),sQuery(id+"F2.wireOp",EDGE,"E20"),sQuery(id+"F2.wireOp",EDGE,"E21"),sQuery(id+"F2.wireOp",EDGE,"E22"),sQuery(id+"F2.wireOp",EDGE,"E23"),sQuery(id+"F2.wireOp",EDGE,"E24"),sQuery(id+"F2.wireOp",EDGE,"E25"),sQuery(id+"F2.wireOp",EDGE,"E26"),sQuery(id+"F2.wireOp",EDGE,"E27"),sQuery(id+"F2.wireOp",EDGE,"E28"),sQuery(id+"F2.wireOp",EDGE,"E29"),sQuery(id+"F2.wireOp",EDGE,"E30"),sQuery(id+"F2.wireOp",EDGE,"E31"),sQuery(id+"F2.wireOp",EDGE,"E32"),sQuery(id+"F2.wireOp",EDGE,"E33"),sQuery(id+"F2.wireOp",EDGE,"E34"),sQuery(id+"F2.wireOp",EDGE,"E35"),sQuery(id+"F2.wireOp",EDGE,"E36"),sQuery(id+"F2.wireOp",EDGE,"E37"),sQuery(id+"F2.wireOp",EDGE,"E38"),sQuery(id+"F2.wireOp",EDGE,"E39"),sQuery(id+"F2.wireOp",EDGE,"E40"),sQuery(id+"F2.wireOp",EDGE,"E41"),sQuery(id+"F2.wireOp",EDGE,"E42"),sQuery(id+"F2.wireOp",EDGE,"E43"),sQuery(id+"F2.wireOp",EDGE,"E44"),sQuery(id+"F2.wireOp",EDGE,"E45"),sQuery(id+"F2.wireOp",EDGE,"E46"),sQuery(id+"F2.wireOp",EDGE,"E47"),sQuery(id+"F2.wireOp",EDGE,"E48"),sQuery(id+"F2.wireOp",EDGE,"E49"),sQuery(id+"F2.wireOp",EDGE,"E50"),sQuery(id+"F2.wireOp",EDGE,"E51"),sQuery(id+"F2.wireOp",EDGE,"E52"),sQuery(id+"F2.wireOp",EDGE,"E53"),sQuery(id+"F2.wireOp",EDGE,"E54"),sQuery(id+"F2.wireOp",EDGE,"E55"),sQuery(id+"F2.wireOp",EDGE,"E56"),sQuery(id+"F2.wireOp",EDGE,"E57"),sQuery(id+"F2.wireOp",EDGE,"E58"),sQuery(id+"F2.wireOp",EDGE,"E59"),sQuery(id+"F2.wireOp",EDGE,"E60"),sQuery(id+"F2.wireOp",EDGE,"E61"),sQuery(id+"F2.wireOp",EDGE,"E62"),sQuery(id+"F2.wireOp",EDGE,"E63"),sQuery(id+"F2.wireOp",EDGE,"E64"),sQuery(id+"F2.wireOp",EDGE,"E65"),sQuery(id+"F2.wireOp",EDGE,"E66"),sQuery(id+"F2.wireOp",EDGE,"E67"),sQuery(id+"F2.wireOp",EDGE,"E68"),sQuery(id+"F2.wireOp",EDGE,"E69"),sQuery(id+"F2.wireOp",EDGE,"E70"),sQuery(id+"F2.wireOp",EDGE,"E71"),sQuery(id+"F2.wireOp",EDGE,"E72"),sQuery(id+"F2.wireOp",EDGE,"E73"),sQuery(id+"F2.wireOp",EDGE,"E74"),sQuery(id+"F2.wireOp",EDGE,"E75"),sQuery(id+"F2.wireOp",EDGE,"E76"),sQuery(id+"F2.wireOp",EDGE,"E77"),sQuery(id+"F2.wireOp",EDGE,"E78"),sQuery(id+"F2.wireOp",EDGE,"E79"),sQuery(id+"F2.wireOp",EDGE,"E80"),sQuery(id+"F2.wireOp",EDGE,"E81"),sQuery(id+"F2.wireOp",EDGE,"E82"),sQuery(id+"F2.wireOp",EDGE,"E83"),sQuery(id+"F2.wireOp",EDGE,"E84"),sQuery(id+"F2.wireOp",EDGE,"E85"),sQuery(id+"F2.wireOp",EDGE,"E86"),sQuery(id+"F2.wireOp",EDGE,"E87"),sQuery(id+"F2.wireOp",EDGE,"E88"),sQuery(id+"F2.wireOp",EDGE,"E89"),sQuery(id+"F2.wireOp",EDGE,"E90"),sQuery(id+"F2.wireOp",EDGE,"E91"),sQuery(id+"F2.wireOp",EDGE,"E92"),sQuery(id+"F2.wireOp",EDGE,"E93"),sQuery(id+"F2.wireOp",EDGE,"E94"),sQuery(id+"F2.wireOp",EDGE,"E95"),sQuery(id+"F2.wireOp",EDGE,"E96"),sQuery(id+"F2.wireOp",EDGE,"E97"),sQuery(id+"F2.wireOp",EDGE,"E98"),sQuery(id+"F2.wireOp",EDGE,"E99"),sQuery(id+"F2.wireOp",EDGE,"E100"),sQuery(id+"F2.wireOp",EDGE,"E101"),sQuery(id+"F2.wireOp",EDGE,"E102"),sQuery(id+"F2.wireOp",EDGE,"E103"),sQuery(id+"F2.wireOp",EDGE,"E104"),sQuery(id+"F2.wireOp",EDGE,"E105"),sQuery(id+"F2.wireOp",EDGE,"E106"),sQuery(id+"F2.wireOp",EDGE,"E107"),sQuery(id+"F2.wireOp",EDGE,"E108"),sQuery(id+"F2.wireOp",EDGE,"E109"),sQuery(id+"F2.wireOp",EDGE,"E110"),sQuery(id+"F2.wireOp",EDGE,"E111"),sQuery(id+"F2.wireOp",EDGE,"E112"),sQuery(id+"F2.wireOp",EDGE,"E113"),sQuery(id+"F2.wireOp",EDGE,"E114"),sQuery(id+"F2.wireOp",EDGE,"E115"),sQuery(id+"F2.wireOp",EDGE,"E116"),sQuery(id+"F2.wireOp",EDGE,"E117"),sQuery(id+"F2.wireOp",EDGE,"E118"),sQuery(id+"F2.wireOp",EDGE,"E119"),sQuery(id+"F2.wireOp",EDGE,"E120"),sQuery(id+"F2.wireOp",EDGE,"E121"),sQuery(id+"F2.wireOp",EDGE,"E122"),sQuery(id+"F2.wireOp",EDGE,"E123"),sQuery(id+"F2.wireOp",EDGE,"E124"),sQuery(id+"F2.wireOp",EDGE,"E125"),sQuery(id+"F2.wireOp",EDGE,"E126"),sQuery(id+"F2.wireOp",EDGE,"E127"),sQuery(id+"F2.wireOp",EDGE,"E128"),sQuery(id+"F2.wireOp",EDGE,"E129"),sQuery(id+"F2.wireOp",EDGE,"E130"),sQuery(id+"F2.wireOp",EDGE,"E131"),sQuery(id+"F2.wireOp",EDGE,"E132"),sQuery(id+"F2.wireOp",EDGE,"E133"),sQuery(id+"F2.wireOp",EDGE,"E134"),sQuery(id+"F2.wireOp",EDGE,"E135"),sQuery(id+"F2.wireOp",EDGE,"E136"),sQuery(id+"F2.wireOp",EDGE,"E137"),sQuery(id+"F2.wireOp",EDGE,"E138"),sQuery(id+"F2.wireOp",EDGE,"E139"),sQuery(id+"F2.wireOp",EDGE,"E140"),sQuery(id+"F2.wireOp",EDGE,"E141"),sQuery(id+"F2.wireOp",EDGE,"E142"),sQuery(id+"F2.wireOp",EDGE,"E143"),sQuery(id+"F2.wireOp",EDGE,"E144"),sQuery(id+"F2.wireOp",EDGE,"E145"),sQuery(id+"F2.wireOp",EDGE,"E146"),sQuery(id+"F2.wireOp",EDGE,"E147"),sQuery(id+"F2.wireOp",EDGE,"E148"),sQuery(id+"F2.wireOp",EDGE,"E149"),sQuery(id+"F2.wireOp",EDGE,"E150"),sQuery(id+"F2.wireOp",EDGE,"E151"),sQuery(id+"F2.wireOp",EDGE,"E152"),sQuery(id+"F2.wireOp",EDGE,"E153"),sQuery(id+"F2.wireOp",EDGE,"E154"),sQuery(id+"F2.wireOp",EDGE,"E155"),sQuery(id+"F2.wireOp",EDGE,"E156"),sQuery(id+"F2.wireOp",EDGE,"E157"),sQuery(id+"F2.wireOp",EDGE,"E158"),sQuery(id+"F2.wireOp",EDGE,"E159"),sQuery(id+"F2.wireOp",EDGE,"E160"),sQuery(id+"F2.wireOp",EDGE,"E161"),sQuery(id+"F2.wireOp",EDGE,"E162"),sQuery(id+"F2.wireOp",EDGE,"E163"),sQuery(id+"F2.wireOp",EDGE,"E164"),sQuery(id+"F2.wireOp",EDGE,"E165"),sQuery(id+"F2.wireOp",EDGE,"E166"),sQuery(id+"F2.wireOp",EDGE,"E167"),sQuery(id+"F2.wireOp",EDGE,"E168"),sQuery(id+"F2.wireOp",EDGE,"E169"),sQuery(id+"F2.wireOp",EDGE,"E170"),sQuery(id+"F2.wireOp",EDGE,"E171"),sQuery(id+"F2.wireOp",EDGE,"E172"),sQuery(id+"F2.wireOp",EDGE,"E173"),sQuery(id+"F2.wireOp",EDGE,"E174"),sQuery(id+"F2.wireOp",EDGE,"E175"),sQuery(id+"F2.wireOp",EDGE,"E176"),sQuery(id+"F2.wireOp",EDGE,"E177"),sQuery(id+"F2.wireOp",EDGE,"E178"),sQuery(id+"F2.wireOp",EDGE,"E179"),sQuery(id+"F2.wireOp",EDGE,"E180"),sQuery(id+"F2.wireOp",EDGE,"E181"),sQuery(id+"F2.wireOp",EDGE,"E182"),sQuery(id+"F2.wireOp",EDGE,"E183"),sQuery(id+"F2.wireOp",EDGE,"E184"),sQuery(id+"F2.wireOp",EDGE,"E185"),sQuery(id+"F2.wireOp",EDGE,"E186"),sQuery(id+"F2.wireOp",EDGE,"E187"),sQuery(id+"F2.wireOp",EDGE,"E188"),sQuery(id+"F2.wireOp",EDGE,"E189"),sQuery(id+"F2.wireOp",EDGE,"E190"),sQuery(id+"F2.wireOp",EDGE,"E191"),sQuery(id+"F2.wireOp",EDGE,"E192"),sQuery(id+"F2.wireOp",EDGE,"E193"),sQuery(id+"F2.wireOp",EDGE,"E194"),sQuery(id+"F2.wireOp",EDGE,"E195"),sQuery(id+"F2.wireOp",EDGE,"E196"),sQuery(id+"F2.wireOp",EDGE,"E197"),sQuery(id+"F2.wireOp",EDGE,"E198"),sQuery(id+"F2.wireOp",EDGE,"E199"),sQuery(id+"F2.wireOp",EDGE,"E200"),sQuery(id+"F2.wireOp",EDGE,"E201"),sQuery(id+"F2.wireOp",EDGE,"E202"),sQuery(id+"F2.wireOp",EDGE,"E203"),sQuery(id+"F2.wireOp",EDGE,"E204"),sQuery(id+"F2.wireOp",EDGE,"E205"),sQuery(id+"F2.wireOp",EDGE,"E206"),sQuery(id+"F2.wireOp",EDGE,"E207"),sQuery(id+"F2.wireOp",EDGE,"E208"),sQuery(id+"F2.wireOp",EDGE,"E209"),sQuery(id+"F2.wireOp",EDGE,"E210"),sQuery(id+"F2.wireOp",EDGE,"E211"),sQuery(id+"F2.wireOp",EDGE,"E212"),sQuery(id+"F2.wireOp",EDGE,"E213"),sQuery(id+"F2.wireOp",EDGE,"E214"),sQuery(id+"F2.wireOp",EDGE,"E215"),sQuery(id+"F2.wireOp",EDGE,"E216"),sQuery(id+"F2.wireOp",EDGE,"E217"),sQuery(id+"F2.wireOp",EDGE,"E218"),sQuery(id+"F2.wireOp",EDGE,"E219"),sQuery(id+"F2.wireOp",EDGE,"E220"),sQuery(id+"F2.wireOp",EDGE,"E221"),sQuery(id+"F2.wireOp",EDGE,"E222"),sQuery(id+"F2.wireOp",EDGE,"E223"),sQuery(id+"F2.wireOp",EDGE,"E224"),sQuery(id+"F2.wireOp",EDGE,"E225"),sQuery(id+"F2.wireOp",EDGE,"E226"),sQuery(id+"F2.wireOp",EDGE,"E227"),sQuery(id+"F2.wireOp",EDGE,"E228"),sQuery(id+"F2.wireOp",EDGE,"E229"),sQuery(id+"F2.wireOp",EDGE,"E230"),sQuery(id+"F2.wireOp",EDGE,"E231"),sQuery(id+"F2.wireOp",EDGE,"E232"),sQuery(id+"F2.wireOp",EDGE,"E233"),sQuery(id+"F2.wireOp",EDGE,"E234"),sQuery(id+"F2.wireOp",EDGE,"E235"),sQuery(id+"F2.wireOp",EDGE,"E236"),sQuery(id+"F2.wireOp",EDGE,"E237"),sQuery(id+"F2.wireOp",EDGE,"E238"),sQuery(id+"F2.wireOp",EDGE,"E239"),sQuery(id+"F2.wireOp",EDGE,"E240"),sQuery(id+"F2.wireOp",EDGE,"E241"),sQuery(id+"F2.wireOp",EDGE,"E242"),sQuery(id+"F2.wireOp",EDGE,"E243"),sQuery(id+"F2.wireOp",EDGE,"E244"),sQuery(id+"F2.wireOp",EDGE,"E245"),sQuery(id+"F2.wireOp",EDGE,"E246"),sQuery(id+"F2.wireOp",EDGE,"E247"),sQuery(id+"F2.wireOp",EDGE,"E248"),sQuery(id+"F2.wireOp",EDGE,"E249"),sQuery(id+"F2.wireOp",EDGE,"E250"),sQuery(id+"F2.wireOp",EDGE,"E251"),sQuery(id+"F2.wireOp",EDGE,"E252"),sQuery(id+"F2.wireOp",EDGE,"E253"),sQuery(id+"F2.wireOp",EDGE,"E254"),sQuery(id+"F2.wireOp",EDGE,"E255"),sQuery(id+"F2.wireOp",EDGE,"E256"),sQuery(id+"F2.wireOp",EDGE,"E257"),sQuery(id+"F2.wireOp",EDGE,"E258"),sQuery(id+"F2.wireOp",EDGE,"E259"),sQuery(id+"F2.wireOp",EDGE,"E260"),sQuery(id+"F2.wireOp",EDGE,"E261"),sQuery(id+"F2.wireOp",EDGE,"E262"),sQuery(id+"F2.wireOp",EDGE,"E263"),sQuery(id+"F2.wireOp",EDGE,"E264"),sQuery(id+"F2.wireOp",EDGE,"E265"),sQuery(id+"F2.wireOp",EDGE,"E266"),sQuery(id+"F2.wireOp",EDGE,"E267"),sQuery(id+"F2.wireOp",EDGE,"E268"),sQuery(id+"F2.wireOp",EDGE,"E269"),sQuery(id+"F2.wireOp",EDGE,"E270"),sQuery(id+"F2.wireOp",EDGE,"E271"),sQuery(id+"F2.wireOp",EDGE,"E272"),sQuery(id+"F2.wireOp",EDGE,"E273"),sQuery(id+"F2.wireOp",EDGE,"E274"),sQuery(id+"F2.wireOp",EDGE,"E275"),sQuery(id+"F2.wireOp",EDGE,"E276"),sQuery(id+"F2.wireOp",EDGE,"E277"),sQuery(id+"F2.wireOp",EDGE,"E278"),sQuery(id+"F2.wireOp",EDGE,"E279"),sQuery(id+"F2.wireOp",EDGE,"E280"),sQuery(id+"F2.wireOp",EDGE,"E281"),sQuery(id+"F2.wireOp",EDGE,"E282"),sQuery(id+"F2.wireOp",EDGE,"E461.bottom"),sQuery(id+"F2.wireOp",EDGE,"E461.top"),sQuery(id+"F2.wireOp",EDGE,"E461.left"),sQuery(id+"F2.wireOp",EDGE,"E461.right")])]});
            transform(context, id + "F4", {"entities" : qUnion([Q0]), "transformType" : TransformType.TRANSLATION_3D, "dx" : 10.8 * mm, "dy" : 0 * mm, "dz" : 4.62 * mm, "makeCopy" : false});
        }
    });
